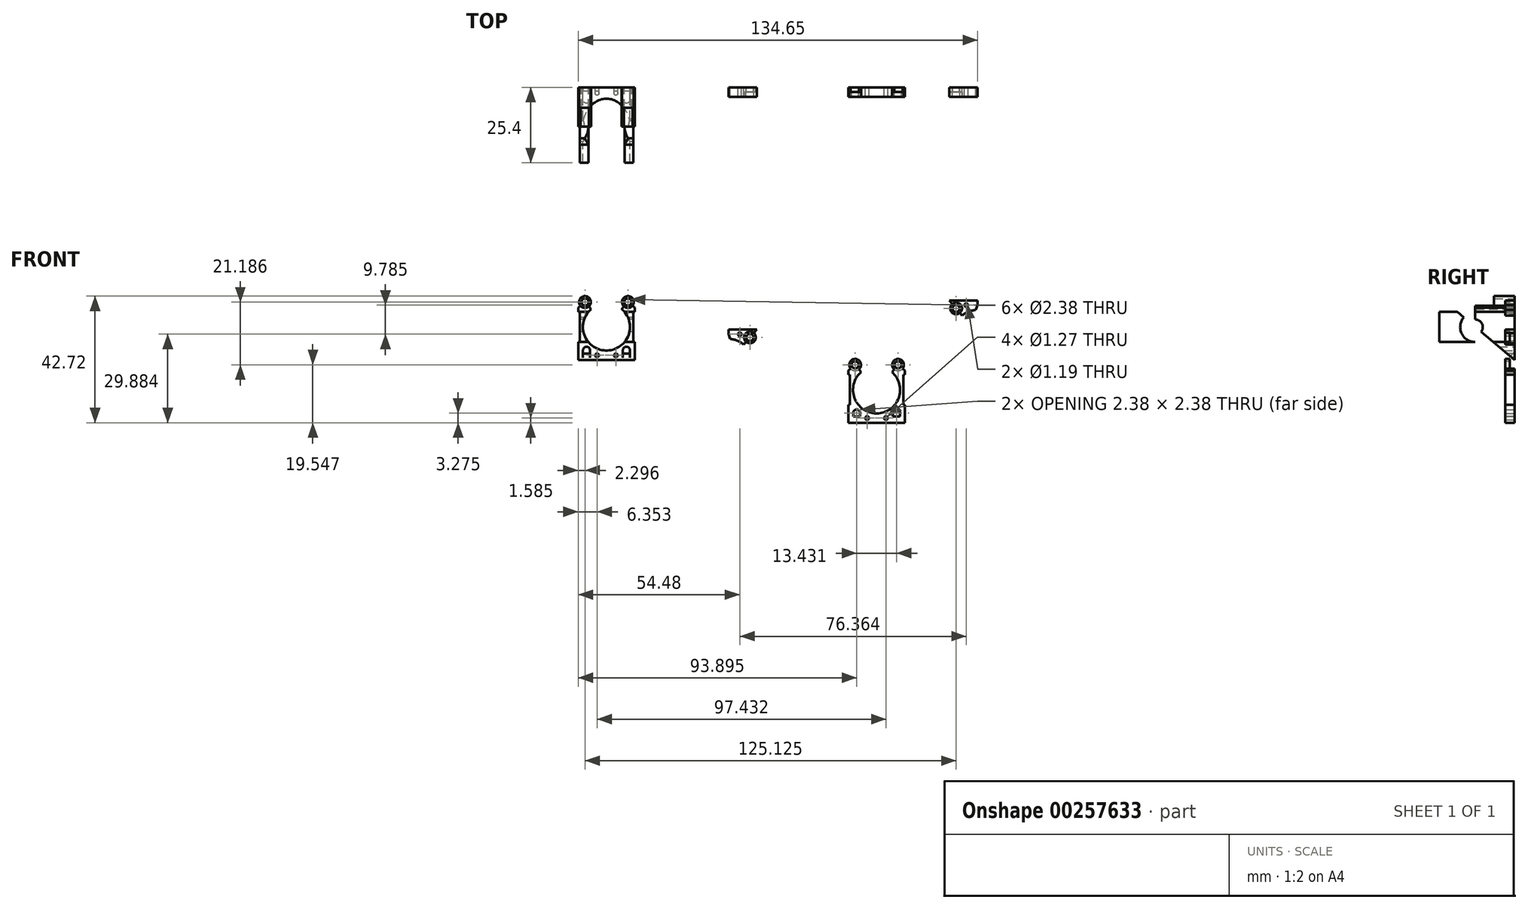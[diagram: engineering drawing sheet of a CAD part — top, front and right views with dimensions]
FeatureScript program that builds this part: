
annotation { "Feature Type Name" : "Feature", "Feature Type Description" : "" }
export const myFeature = defineFeature(function(context is Context, id is Id, definition is map)
    precondition{}
    {
        {
            var Q0;
            Q0=qCreatedBy(makeId("Front.planeOp"),FACE);
            var sketch = newSketch(context, id + "F0", { "sketchPlane" : qUnion([Q0])});
            skArc(sketch, "E0", {"start": v(-0.59, 7.92) * mm, "mid": v(0, -7.94) * mm, "end": v(0.59, 7.92) * mm});
            skCircle(sketch, "E1", {"center": v(0, 0) * mm, "radius": 9.53 * mm, "construction": true});
            skLineSegment(sketch, "E2", {"start": v(-12.11, 0) * mm, "end": v(13.66, 0) * mm, "construction": true});
            skLineSegment(sketch, "E3", {"start": v(0, 12.88) * mm, "end": v(0, -11.87) * mm, "construction": true});
            skLineSegment(sketch, "E4", {"start": v(7.94, 0) * mm, "end": v(7.94, 2.38) * mm, "construction": true});
            skLineSegment(sketch, "E5", {"start": v(9.53, 0) * mm, "end": v(9.53, 2.38) * mm, "construction": true});
            skLineSegment(sketch, "E6.bottom", {"start": v(-9.53, 0) * mm, "end": v(9.53, 0) * mm});
            skLineSegment(sketch, "E6.top", {"start": v(-9.53, 11.11) * mm, "end": v(9.53, 11.11) * mm});
            skLineSegment(sketch, "E6.right", {"start": v(9.53, 0) * mm, "end": v(9.53, 2.38) * mm});
            skLineSegment(sketch, "E7.top", {"start": v(-9.53, -11.11) * mm, "end": v(9.53, -11.11) * mm});
            skLineSegment(sketch, "E7.left", {"start": v(-9.53, -5.08) * mm, "end": v(-9.53, -11.11) * mm});
            skLineSegment(sketch, "E7.right", {"start": v(9.53, -5.08) * mm, "end": v(9.53, -11.11) * mm});
            skLineSegment(sketch, "E8", {"start": v(0, 9.53) * mm, "end": v(5.22, 9.53) * mm, "construction": true});
            skLineSegment(sketch, "E9", {"start": v(-3.97, -9.53) * mm, "end": v(0, -9.53) * mm, "construction": true});
            skLineSegment(sketch, "E10", {"start": v(0, 0) * mm, "end": v(-9.53, 11.11) * mm, "construction": true});
            skLineSegment(sketch, "E11", {"start": v(0, 0) * mm, "end": v(9.53, 11.11) * mm, "construction": true});
            skLineSegment(sketch, "E12", {"start": v(0, 0) * mm, "end": v(9.53, -11.11) * mm, "construction": true});
            skLineSegment(sketch, "E13", {"start": v(0, 0) * mm, "end": v(-9.53, -11.11) * mm, "construction": true});
            skCircle(sketch, "E14", {"center": v(0, 0) * mm, "radius": 11.11 * mm, "construction": true});
            skLineSegment(sketch, "E15", {"start": v(11.11, 0) * mm, "end": v(11.11, -2.7) * mm, "construction": true});
            skLineSegment(sketch, "E16", {"start": v(7.94, 0) * mm, "end": v(7.94, -2.67) * mm, "construction": true});
            skCircle(sketch, "E17", {"center": v(-7.23, 8.44) * mm, "radius": 1.2 * mm});
            skCircle(sketch, "E18", {"center": v(7.23, 8.44) * mm, "radius": 1.2 * mm});
            skCircle(sketch, "E19", {"center": v(-7.23, 8.44) * mm, "radius": 1.98 * mm});
            skCircle(sketch, "E20", {"center": v(7.23, 8.44) * mm, "radius": 1.98 * mm});
            skLineSegment(sketch, "E21", {"start": v(0, 9.53) * mm, "end": v(-5.07, 9.53) * mm, "construction": true});
            skCircle(sketch, "E22", {"center": v(-3.81, 9.53) * mm, "radius": 0.6 * mm});
            skCircle(sketch, "E23", {"center": v(3.81, 9.53) * mm, "radius": 0.6 * mm});
            skLineSegment(sketch, "E24", {"start": v(-7.23, 8.44) * mm, "end": v(-10.51, 5.63) * mm, "construction": true});
            skLineSegment(sketch, "E25", {"start": v(7.23, 8.44) * mm, "end": v(10.07, 6) * mm, "construction": true});
            skLineSegment(sketch, "E26", {"start": v(-7.23, 8.44) * mm, "end": v(-9.53, 11.11) * mm});
            skLineSegment(sketch, "E27", {"start": v(7.23, 8.44) * mm, "end": v(9.53, 11.11) * mm});
            skLineSegment(sketch, "E28", {"start": v(7.23, 8.44) * mm, "end": v(9.53, 6.47) * mm});
            skLineSegment(sketch, "E29", {"start": v(-7.23, 8.44) * mm, "end": v(-9.53, 6.47) * mm});
            skLineSegment(sketch, "E30", {"start": v(-7.23, 8.44) * mm, "end": v(-5.17, 6.03) * mm});
            skLineSegment(sketch, "E31", {"start": v(7.23, 8.44) * mm, "end": v(5.17, 6.03) * mm});
            skCircle(sketch, "E32", {"center": v(0, 0) * mm, "radius": 10.32 * mm, "construction": true});
            skLineSegment(sketch, "E33", {"start": v(0, -10.32) * mm, "end": v(2.62, -10.32) * mm, "construction": true});
            skCircle(sketch, "E34", {"center": v(6.72, -7.83) * mm, "radius": 1.2 * mm});
            skCircle(sketch, "E35", {"center": v(-6.72, -7.83) * mm, "radius": 1.2 * mm});
            skCircle(sketch, "E36", {"center": v(6.72, -7.83) * mm, "radius": 1.98 * mm});
            skCircle(sketch, "E37", {"center": v(-6.72, -7.83) * mm, "radius": 1.98 * mm});
            skLineSegment(sketch, "E38", {"start": v(-4.44, -7.83) * mm, "end": v(-9.1, -7.83) * mm, "construction": true});
            skLineSegment(sketch, "E39", {"start": v(8.94, -7.83) * mm, "end": v(4.4, -7.83) * mm, "construction": true});
            skLineSegment(sketch, "E40.bottom", {"start": v(-7.9, -7.83) * mm, "end": v(-6.72, -7.83) * mm});
            skLineSegment(sketch, "E40.top", {"start": v(-7.9, -9.03) * mm, "end": v(-6.72, -9.03) * mm});
            skLineSegment(sketch, "E40.left", {"start": v(-7.9, -7.83) * mm, "end": v(-7.9, -9.03) * mm});
            skLineSegment(sketch, "E40.right", {"start": v(-6.72, -7.83) * mm, "end": v(-6.72, -9.03) * mm});
            skLineSegment(sketch, "E41.bottom", {"start": v(-6.72, -9.03) * mm, "end": v(-5.52, -9.03) * mm});
            skLineSegment(sketch, "E41.top", {"start": v(-6.72, -7.83) * mm, "end": v(-5.52, -7.83) * mm});
            skLineSegment(sketch, "E41.left", {"start": v(-6.72, -9.03) * mm, "end": v(-6.72, -7.83) * mm});
            skLineSegment(sketch, "E41.right", {"start": v(-5.52, -9.03) * mm, "end": v(-5.52, -7.83) * mm});
            skLineSegment(sketch, "E42.bottom", {"start": v(5.52, -7.83) * mm, "end": v(6.72, -7.83) * mm});
            skLineSegment(sketch, "E42.top", {"start": v(5.52, -9.03) * mm, "end": v(6.72, -9.03) * mm});
            skLineSegment(sketch, "E42.left", {"start": v(5.52, -7.83) * mm, "end": v(5.52, -9.03) * mm});
            skLineSegment(sketch, "E42.right", {"start": v(6.72, -7.83) * mm, "end": v(6.72, -9.03) * mm});
            skLineSegment(sketch, "E43.bottom", {"start": v(6.72, -9.03) * mm, "end": v(7.9, -9.03) * mm});
            skLineSegment(sketch, "E43.top", {"start": v(6.72, -7.83) * mm, "end": v(7.9, -7.83) * mm});
            skLineSegment(sketch, "E43.left", {"start": v(6.72, -9.03) * mm, "end": v(6.72, -7.83) * mm});
            skLineSegment(sketch, "E43.right", {"start": v(7.9, -9.03) * mm, "end": v(7.9, -7.83) * mm});
            skLineSegment(sketch, "E44", {"start": v(0, -9.53) * mm, "end": v(4.87, -9.53) * mm, "construction": true});
            skCircle(sketch, "E45", {"center": v(-3.17, -9.53) * mm, "radius": 0.64 * mm});
            skCircle(sketch, "E46", {"center": v(3.18, -9.53) * mm, "radius": 0.64 * mm});
            skLineSegment(sketch, "E47", {"start": v(0, 9.53) * mm, "end": v(0.59, 7.92) * mm});
            skLineSegment(sketch, "E48", {"start": v(0, 9.53) * mm, "end": v(-0.59, 7.92) * mm});
            skLineSegment(sketch, "E49.bottom", {"start": v(-9.53, 5.08) * mm, "end": v(-9.02, 5.08) * mm});
            skLineSegment(sketch, "E49.top", {"start": v(-9.52, -5.08) * mm, "end": v(-9.02, -5.08) * mm});
            skLineSegment(sketch, "E49.right", {"start": v(-9.02, 5.08) * mm, "end": v(-9.02, -5.08) * mm});
            skPoint(sketch, "E50.firstSnap0", {"position": v(-9.27, 5.08) * mm});
            skLineSegment(sketch, "E50.bottom", {"start": v(9.53, 5.08) * mm, "end": v(9.02, 5.08) * mm});
            skLineSegment(sketch, "E50.top", {"start": v(9.52, -5.08) * mm, "end": v(9.02, -5.08) * mm});
            skLineSegment(sketch, "E50.right", {"start": v(9.02, 5.08) * mm, "end": v(9.02, -5.08) * mm});
            skLineSegment(sketch, "E51.trimOffspring", {"start": v(-9.53, 5.08) * mm, "end": v(-9.53, 6.47) * mm});
            skLineSegment(sketch, "E52.trimOffspring", {"start": v(9.53, 5.08) * mm, "end": v(9.53, 6.47) * mm});
            skLineSegment(sketch, "E53", {"start": v(0, 9.53) * mm, "end": v(0, 11.11) * mm});
            skSolve(sketch);
        }
        {
            var Q0;
            {var subQ7=sQuery(id+"F0.wireOp",EDGE,"E50.bottom");Q0=makeQuery(id+"F0.imprint","IMPRINT",FACE,{"disambiguationData":[TD([[makeQuery(id+"F0.imprint","IMPRINT",EDGE,{"derivedFrom":subQ7}),-1.0]])]});}
            var Q1;
            {var subQ12=sQuery(id+"F0.wireOp",EDGE,"E49.bottom");Q1=makeQuery(id+"F0.imprint","IMPRINT",FACE,{"disambiguationData":[TD([[makeQuery(id+"F0.imprint","IMPRINT",EDGE,{"derivedFrom":subQ12}),1.0]])]});}
            var Q2;
            Q2=makeQuery(id+"F0.imprint","IMPRINT",FACE,{"disambiguationData":[TD([[makeQuery(id+"F0.imprint","IMPRINT",EDGE,{"derivedFrom":sQuery(id+"F0.wireOp",EDGE,"E7.top")}),1.0]])]});
            var Q3;
            {var subQ0=sQuery(id+"F0.wireOp",EDGE,"E27");var subQ1=sQuery(id+"F0.wireOp",EDGE,"E18");var subQ2=makeQuery(id+"F0.imprint","INTERSECT",VERTEX,{"derivedFrom":[subQ1,subQ0]});Q3=makeQuery(id+"F0.imprint","IMPRINT",FACE,{"disambiguationData":[TD([[makeQuery(id+"F0.imprint","IMPRINT",EDGE,{"disambiguationData":[TD([[subQ2,1.0]])],"derivedFrom":subQ1}),-1.0]])]});}
            var Q4;
            {var subQ0=sQuery(id+"F0.wireOp",EDGE,"E31");var subQ1=sQuery(id+"F0.wireOp",EDGE,"E18");var subQ2=makeQuery(id+"F0.imprint","INTERSECT",VERTEX,{"derivedFrom":[subQ1,subQ0]});Q4=makeQuery(id+"F0.imprint","IMPRINT",FACE,{"disambiguationData":[TD([[makeQuery(id+"F0.imprint","IMPRINT",EDGE,{"disambiguationData":[TD([[subQ2,1.0]])],"derivedFrom":subQ1}),-1.0]])]});}
            var Q5;
            {var subQ0=sQuery(id+"F0.wireOp",EDGE,"E31");var subQ1=sQuery(id+"F0.wireOp",EDGE,"E18");var subQ2=makeQuery(id+"F0.imprint","INTERSECT",VERTEX,{"derivedFrom":[subQ1,subQ0]});Q5=makeQuery(id+"F0.imprint","IMPRINT",FACE,{"disambiguationData":[TD([[makeQuery(id+"F0.imprint","IMPRINT",EDGE,{"disambiguationData":[TD([[subQ2,-1.0]])],"derivedFrom":subQ1}),-1.0]])]});}
            var Q6;
            {var subQ0=sQuery(id+"F0.wireOp",EDGE,"E26");var subQ1=sQuery(id+"F0.wireOp",EDGE,"E17");var subQ2=makeQuery(id+"F0.imprint","INTERSECT",VERTEX,{"derivedFrom":[subQ1,subQ0]});Q6=makeQuery(id+"F0.imprint","IMPRINT",FACE,{"disambiguationData":[TD([[makeQuery(id+"F0.imprint","IMPRINT",EDGE,{"disambiguationData":[TD([[subQ2,1.0]])],"derivedFrom":subQ1}),-1.0]])]});}
            var Q7;
            {var subQ0=sQuery(id+"F0.wireOp",EDGE,"E29");var subQ1=sQuery(id+"F0.wireOp",EDGE,"E17");var subQ2=makeQuery(id+"F0.imprint","INTERSECT",VERTEX,{"derivedFrom":[subQ1,subQ0]});Q7=makeQuery(id+"F0.imprint","IMPRINT",FACE,{"disambiguationData":[TD([[makeQuery(id+"F0.imprint","IMPRINT",EDGE,{"disambiguationData":[TD([[subQ2,1.0]])],"derivedFrom":subQ1}),-1.0]])]});}
            var Q8;
            {var subQ0=sQuery(id+"F0.wireOp",EDGE,"E29");var subQ1=sQuery(id+"F0.wireOp",EDGE,"E17");var subQ2=makeQuery(id+"F0.imprint","INTERSECT",VERTEX,{"derivedFrom":[subQ1,subQ0]});Q8=makeQuery(id+"F0.imprint","IMPRINT",FACE,{"disambiguationData":[TD([[makeQuery(id+"F0.imprint","IMPRINT",EDGE,{"disambiguationData":[TD([[subQ2,-1.0]])],"derivedFrom":subQ1}),-1.0]])]});}
            var Q9;
            Q9=makeQuery(id+"F0.imprint","IMPRINT",FACE,{"disambiguationData":[TD([[makeQuery(id+"F0.imprint","IMPRINT",EDGE,{"derivedFrom":sQuery(id+"F0.wireOp",EDGE,"E37")}),1.0]])]});
            var Q10;
            Q10=makeQuery(id+"F0.imprint","IMPRINT",FACE,{"disambiguationData":[TD([[makeQuery(id+"F0.imprint","IMPRINT",EDGE,{"derivedFrom":sQuery(id+"F0.wireOp",EDGE,"E36")}),1.0]])]});
            extrude(context, id + "F1", {"entities" : qUnion([Q0, Q1, Q2, Q3, Q4, Q5, Q6, Q7, Q8, Q9, Q10]), "depth" : 3.17 * mm});
        }
        {
            var Q0;
            Q0=makeQuery(id+"F1.opExtrude","CAP_FACE",FACE,{"disambiguationData":[OSD([sQuery(id+"F0.wireOp",EDGE,"E0"),sQuery(id+"F0.wireOp",EDGE,"E7.top"),sQuery(id+"F0.wireOp",EDGE,"E7.left"),sQuery(id+"F0.wireOp",EDGE,"E7.right"),sQuery(id+"F0.wireOp",EDGE,"E17"),sQuery(id+"F0.wireOp",EDGE,"E18"),sQuery(id+"F0.wireOp",EDGE,"E19"),sQuery(id+"F0.wireOp",EDGE,"E20"),sQuery(id+"F0.wireOp",EDGE,"E28"),sQuery(id+"F0.wireOp",EDGE,"E29"),sQuery(id+"F0.wireOp",EDGE,"E30"),sQuery(id+"F0.wireOp",EDGE,"E31"),sQuery(id+"F0.wireOp",EDGE,"E34"),sQuery(id+"F0.wireOp",EDGE,"E35"),sQuery(id+"F0.wireOp",EDGE,"E40.top"),sQuery(id+"F0.wireOp",EDGE,"E40.left"),sQuery(id+"F0.wireOp",EDGE,"E41.bottom"),sQuery(id+"F0.wireOp",EDGE,"E41.right"),sQuery(id+"F0.wireOp",EDGE,"E42.top"),sQuery(id+"F0.wireOp",EDGE,"E42.left"),sQuery(id+"F0.wireOp",EDGE,"E43.bottom"),sQuery(id+"F0.wireOp",EDGE,"E43.right"),sQuery(id+"F0.wireOp",EDGE,"M6doSYil-dpmw-CiuU-3Rmr-2oMEXfOB3LK3"),sQuery(id+"F0.wireOp",EDGE,"LvhBBIzl-iPnS-g3sW-ETMN-LpCGhFxqwUK0"),sQuery(id+"F0.wireOp",EDGE,"E45"),sQuery(id+"F0.wireOp",EDGE,"E46"),sQuery(id+"F0.wireOp",EDGE,"E49.bottom"),sQuery(id+"F0.wireOp",EDGE,"E49.top"),sQuery(id+"F0.wireOp",EDGE,"E49.right"),sQuery(id+"F0.wireOp",EDGE,"E50.bottom"),sQuery(id+"F0.wireOp",EDGE,"E50.top"),sQuery(id+"F0.wireOp",EDGE,"E50.right"),sQuery(id+"F0.wireOp",EDGE,"E51.trimOffspring"),sQuery(id+"F0.wireOp",EDGE,"E52.trimOffspring")])],"isStart":true});
            var sketch = newSketch(context, id + "F2", { "sketchPlane" : qUnion([Q0])});
            skCircle(sketch, "E54", {"center": v(-7.23, 8.44) * mm, "radius": 1.98 * mm});
            skCircle(sketch, "E55", {"center": v(7.23, 8.44) * mm, "radius": 1.98 * mm});
            skSolve(sketch);
        }
        {
            var Q0;
            Q0 = qSketchRegion(id + "F2", true);
            extrude(context, id + "F3", {"entities" : qUnion([Q0]), "operationType" : NewBodyOperationType.REMOVE, "oppositeDirection" : true, "depth" : 1.59 * mm});
        }
        {
            var Q0;
            Q0=qCreatedBy(makeId("Front.planeOp"),FACE);
            var sketch = newSketch(context, id + "F4", { "sketchPlane" : qUnion([Q0])});
            skArc(sketch, "E56", {"start": v(-50.53, 17.17) * mm, "mid": v(-49.94, 1.31) * mm, "end": v(-49.35, 17.17) * mm});
            skCircle(sketch, "E57", {"center": v(-49.94, 9.25) * mm, "radius": 9.53 * mm, "construction": true});
            skLineSegment(sketch, "E58", {"start": v(-62.05, 9.25) * mm, "end": v(-36.28, 9.25) * mm, "construction": true});
            skLineSegment(sketch, "E59", {"start": v(-49.94, 22.13) * mm, "end": v(-49.94, -2.62) * mm, "construction": true});
            skLineSegment(sketch, "E60", {"start": v(-42, 9.25) * mm, "end": v(-42, 11.63) * mm, "construction": true});
            skLineSegment(sketch, "E61", {"start": v(-40.42, 9.25) * mm, "end": v(-40.42, 11.63) * mm, "construction": true});
            skLineSegment(sketch, "E62.bottom", {"start": v(-59.47, 9.25) * mm, "end": v(-40.42, 9.25) * mm});
            skLineSegment(sketch, "E62.top", {"start": v(-59.47, 20.36) * mm, "end": v(-40.42, 20.36) * mm});
            skLineSegment(sketch, "E62.right", {"start": v(-40.42, 9.25) * mm, "end": v(-40.42, 11.63) * mm});
            skLineSegment(sketch, "E63.top", {"start": v(-57.85, -1.86) * mm, "end": v(-42.03, -1.86) * mm});
            skLineSegment(sketch, "E63.left", {"start": v(-59.47, 4.17) * mm, "end": v(-59.47, -0.24) * mm});
            skLineSegment(sketch, "E63.right", {"start": v(-40.42, 4.17) * mm, "end": v(-40.42, -0.24) * mm});
            skLineSegment(sketch, "E64", {"start": v(-49.94, 18.77) * mm, "end": v(-44.72, 18.77) * mm, "construction": true});
            skLineSegment(sketch, "E65", {"start": v(-53.9, -0.28) * mm, "end": v(-49.94, -0.28) * mm, "construction": true});
            skLineSegment(sketch, "E66", {"start": v(-49.94, 9.25) * mm, "end": v(-59.47, 20.36) * mm, "construction": true});
            skLineSegment(sketch, "E67", {"start": v(-49.94, 9.25) * mm, "end": v(-40.42, 20.36) * mm, "construction": true});
            skLineSegment(sketch, "E68", {"start": v(-49.94, 9.25) * mm, "end": v(-40.42, -1.86) * mm, "construction": true});
            skLineSegment(sketch, "E69", {"start": v(-49.94, 9.25) * mm, "end": v(-59.47, -1.86) * mm, "construction": true});
            skCircle(sketch, "E70", {"center": v(-49.94, 9.25) * mm, "radius": 11.11 * mm, "construction": true});
            skLineSegment(sketch, "E71", {"start": v(-38.83, 9.25) * mm, "end": v(-38.83, 6.55) * mm, "construction": true});
            skLineSegment(sketch, "E72", {"start": v(-42, 9.25) * mm, "end": v(-42, 6.58) * mm, "construction": true});
            skCircle(sketch, "E73", {"center": v(-57.17, 17.69) * mm, "radius": 1.2 * mm});
            skCircle(sketch, "E74", {"center": v(-42.7, 17.69) * mm, "radius": 1.2 * mm});
            skCircle(sketch, "E75", {"center": v(-57.17, 17.69) * mm, "radius": 1.98 * mm});
            skCircle(sketch, "E76", {"center": v(-42.7, 17.69) * mm, "radius": 1.98 * mm});
            skLineSegment(sketch, "E77", {"start": v(-49.94, 18.77) * mm, "end": v(-55.01, 18.77) * mm, "construction": true});
            skCircle(sketch, "E78", {"center": v(-53.75, 18.77) * mm, "radius": 0.6 * mm});
            skCircle(sketch, "E79", {"center": v(-46.13, 18.77) * mm, "radius": 0.6 * mm});
            skLineSegment(sketch, "E80", {"start": v(-57.17, 17.69) * mm, "end": v(-60.45, 14.88) * mm, "construction": true});
            skLineSegment(sketch, "E81", {"start": v(-42.7, 17.69) * mm, "end": v(-39.87, 15.26) * mm, "construction": true});
            skLineSegment(sketch, "E82", {"start": v(-57.17, 17.69) * mm, "end": v(-59.47, 20.36) * mm});
            skLineSegment(sketch, "E83", {"start": v(-42.7, 17.69) * mm, "end": v(-40.42, 20.36) * mm});
            skLineSegment(sketch, "E84", {"start": v(-42.7, 17.69) * mm, "end": v(-40.42, 15.72) * mm});
            skLineSegment(sketch, "E85", {"start": v(-57.17, 17.69) * mm, "end": v(-59.47, 15.72) * mm});
            skLineSegment(sketch, "E86", {"start": v(-57.17, 17.69) * mm, "end": v(-55.1, 15.28) * mm});
            skLineSegment(sketch, "E87", {"start": v(-42.7, 17.69) * mm, "end": v(-44.77, 15.28) * mm});
            skCircle(sketch, "E88", {"center": v(-49.94, 9.25) * mm, "radius": 10.32 * mm, "construction": true});
            skLineSegment(sketch, "E89", {"start": v(-49.94, -1.07) * mm, "end": v(-47.32, -1.07) * mm, "construction": true});
            skCircle(sketch, "E90", {"center": v(-43.22, 1.41) * mm, "radius": 1.2 * mm});
            skCircle(sketch, "E91", {"center": v(-56.66, 1.41) * mm, "radius": 1.2 * mm});
            skCircle(sketch, "E92", {"center": v(-43.22, 1.41) * mm, "radius": 1.98 * mm});
            skCircle(sketch, "E93", {"center": v(-56.66, 1.41) * mm, "radius": 1.98 * mm});
            skLineSegment(sketch, "E94", {"start": v(-54.38, 1.41) * mm, "end": v(-59.04, 1.41) * mm, "construction": true});
            skLineSegment(sketch, "E95", {"start": v(-41, 1.41) * mm, "end": v(-45.53, 1.41) * mm, "construction": true});
            skLineSegment(sketch, "E96.bottom", {"start": v(-57.85, 1.41) * mm, "end": v(-56.66, 1.41) * mm});
            skLineSegment(sketch, "E96.top", {"start": v(-57.85, 0.22) * mm, "end": v(-56.66, 0.22) * mm});
            skLineSegment(sketch, "E96.left", {"start": v(-57.85, 1.41) * mm, "end": v(-57.85, 0.22) * mm});
            skLineSegment(sketch, "E96.right", {"start": v(-56.66, 1.41) * mm, "end": v(-56.66, 0.22) * mm});
            skLineSegment(sketch, "E97.bottom", {"start": v(-56.66, 0.22) * mm, "end": v(-55.46, 0.22) * mm});
            skLineSegment(sketch, "E97.top", {"start": v(-56.66, 1.41) * mm, "end": v(-55.46, 1.41) * mm});
            skLineSegment(sketch, "E97.left", {"start": v(-56.66, 0.22) * mm, "end": v(-56.66, 1.41) * mm});
            skLineSegment(sketch, "E97.right", {"start": v(-55.46, 0.22) * mm, "end": v(-55.46, 1.41) * mm});
            skLineSegment(sketch, "E98.bottom", {"start": v(-44.42, 1.41) * mm, "end": v(-43.22, 1.41) * mm});
            skLineSegment(sketch, "E98.top", {"start": v(-44.42, 0.22) * mm, "end": v(-43.22, 0.22) * mm});
            skLineSegment(sketch, "E98.left", {"start": v(-44.42, 1.41) * mm, "end": v(-44.42, 0.22) * mm});
            skLineSegment(sketch, "E98.right", {"start": v(-43.22, 1.41) * mm, "end": v(-43.22, 0.22) * mm});
            skLineSegment(sketch, "E99.bottom", {"start": v(-43.22, 0.22) * mm, "end": v(-42.03, 0.22) * mm});
            skLineSegment(sketch, "E99.top", {"start": v(-43.22, 1.41) * mm, "end": v(-42.03, 1.41) * mm});
            skLineSegment(sketch, "E99.left", {"start": v(-43.22, 0.22) * mm, "end": v(-43.22, 1.41) * mm});
            skLineSegment(sketch, "E99.right", {"start": v(-42.03, 0.22) * mm, "end": v(-42.03, 1.41) * mm});
            skLineSegment(sketch, "E100", {"start": v(-57.85, -1.86) * mm, "end": v(-59.47, -0.24) * mm});
            skLineSegment(sketch, "E101", {"start": v(-42.03, -1.86) * mm, "end": v(-40.42, -0.24) * mm});
            skLineSegment(sketch, "E102", {"start": v(-49.94, -0.28) * mm, "end": v(-45.07, -0.28) * mm, "construction": true});
            skCircle(sketch, "E103", {"center": v(-53.12, -0.28) * mm, "radius": 0.64 * mm});
            skCircle(sketch, "E104", {"center": v(-46.77, -0.28) * mm, "radius": 0.64 * mm});
            skLineSegment(sketch, "E105", {"start": v(-49.94, 18.77) * mm, "end": v(-49.35, 17.17) * mm});
            skLineSegment(sketch, "E106", {"start": v(-49.94, 18.77) * mm, "end": v(-50.53, 17.17) * mm});
            skLineSegment(sketch, "E107.bottom", {"start": v(-59.47, 14.33) * mm, "end": v(-58.96, 14.33) * mm});
            skLineSegment(sketch, "E107.top", {"start": v(-59.47, 4.17) * mm, "end": v(-58.96, 4.17) * mm});
            skLineSegment(sketch, "E107.right", {"start": v(-58.96, 14.33) * mm, "end": v(-58.96, 4.17) * mm});
            skPoint(sketch, "E108.firstSnap0", {"position": v(-59.21, 14.33) * mm});
            skLineSegment(sketch, "E108.bottom", {"start": v(-40.42, 14.33) * mm, "end": v(-40.92, 14.33) * mm});
            skLineSegment(sketch, "E108.top", {"start": v(-40.42, 4.17) * mm, "end": v(-40.92, 4.17) * mm});
            skLineSegment(sketch, "E108.right", {"start": v(-40.92, 14.33) * mm, "end": v(-40.92, 4.17) * mm});
            skLineSegment(sketch, "E109.trimOffspring", {"start": v(-59.47, 14.33) * mm, "end": v(-59.47, 15.72) * mm});
            skLineSegment(sketch, "E110.trimOffspring", {"start": v(-40.42, 14.33) * mm, "end": v(-40.42, 15.72) * mm});
            skLineSegment(sketch, "E111", {"start": v(-49.94, 18.77) * mm, "end": v(-49.94, 20.36) * mm});
            skSolve(sketch);
        }
        {
            var Q0;
            {var subQ0=sQuery(id+"F4.wireOp",EDGE,"E83");var subQ1=sQuery(id+"F4.wireOp",EDGE,"E74");var subQ2=makeQuery(id+"F4.imprint","INTERSECT",VERTEX,{"derivedFrom":[subQ1,subQ0]});Q0=makeQuery(id+"F4.imprint","IMPRINT",FACE,{"disambiguationData":[TD([[makeQuery(id+"F4.imprint","IMPRINT",EDGE,{"disambiguationData":[TD([[subQ2,1.0]])],"derivedFrom":subQ1}),-1.0]])]});}
            var Q1;
            {var subQ0=sQuery(id+"F4.wireOp",EDGE,"E87");var subQ1=sQuery(id+"F4.wireOp",EDGE,"E74");var subQ2=makeQuery(id+"F4.imprint","INTERSECT",VERTEX,{"derivedFrom":[subQ1,subQ0]});Q1=makeQuery(id+"F4.imprint","IMPRINT",FACE,{"disambiguationData":[TD([[makeQuery(id+"F4.imprint","IMPRINT",EDGE,{"disambiguationData":[TD([[subQ2,1.0]])],"derivedFrom":subQ1}),-1.0]])]});}
            var Q2;
            {var subQ0=sQuery(id+"F4.wireOp",EDGE,"E87");var subQ1=sQuery(id+"F4.wireOp",EDGE,"E74");var subQ2=makeQuery(id+"F4.imprint","INTERSECT",VERTEX,{"derivedFrom":[subQ1,subQ0]});Q2=makeQuery(id+"F4.imprint","IMPRINT",FACE,{"disambiguationData":[TD([[makeQuery(id+"F4.imprint","IMPRINT",EDGE,{"disambiguationData":[TD([[subQ2,-1.0]])],"derivedFrom":subQ1}),-1.0]])]});}
            var Q3;
            Q3=makeQuery(id+"F4.imprint","IMPRINT",FACE,{"disambiguationData":[TD([[makeQuery(id+"F4.imprint","IMPRINT",EDGE,{"derivedFrom":sQuery(id+"F4.wireOp",EDGE,"E79")}),-1.0]])]});
            extrude(context, id + "F5", {"entities" : qUnion([Q0, Q1, Q2, Q3]), "depth" : 3.17 * mm});
        }
        {
            var Q0;
            Q0=makeQuery(id+"F5.opExtrude","CAP_FACE",FACE,{"disambiguationData":[OSD([sQuery(id+"F4.wireOp",EDGE,"E56"),sQuery(id+"F4.wireOp",EDGE,"E62.top"),sQuery(id+"F4.wireOp",EDGE,"E74"),sQuery(id+"F4.wireOp",EDGE,"E76"),sQuery(id+"F4.wireOp",EDGE,"E79"),sQuery(id+"F4.wireOp",EDGE,"E83"),sQuery(id+"F4.wireOp",EDGE,"E87"),sQuery(id+"F4.wireOp",EDGE,"E105"),sQuery(id+"F4.wireOp",EDGE,"E111")])],"isStart":false});
            var sketch = newSketch(context, id + "F6", { "sketchPlane" : qUnion([Q0])});
            skCircle(sketch, "E112", {"center": v(-42.7, 17.69) * mm, "radius": 1.98 * mm});
            skSolve(sketch);
        }
        {
            var Q0;
            Q0 = qSketchRegion(id + "F6", true);
            extrude(context, id + "F7", {"entities" : qUnion([Q0]), "operationType" : NewBodyOperationType.REMOVE, "oppositeDirection" : true, "depth" : 1.59 * mm});
        }
        {
            var Q0;
            Q0=qCreatedBy(makeId("Front.planeOp"),FACE);
            var sketch = newSketch(context, id + "F8", { "sketchPlane" : qUnion([Q0])});
            skArc(sketch, "E113", {"start": v(33.46, 26.95) * mm, "mid": v(34.04, 11.1) * mm, "end": v(34.63, 26.95) * mm});
            skCircle(sketch, "E114", {"center": v(34.04, 19.03) * mm, "radius": 9.53 * mm, "construction": true});
            skLineSegment(sketch, "E115", {"start": v(21.93, 19.03) * mm, "end": v(47.7, 19.03) * mm, "construction": true});
            skLineSegment(sketch, "E116", {"start": v(34.04, 31.91) * mm, "end": v(34.04, 7.16) * mm, "construction": true});
            skLineSegment(sketch, "E117", {"start": v(41.98, 19.03) * mm, "end": v(41.98, 21.41) * mm, "construction": true});
            skLineSegment(sketch, "E118", {"start": v(43.57, 19.03) * mm, "end": v(43.57, 21.41) * mm, "construction": true});
            skLineSegment(sketch, "E119.bottom", {"start": v(24.52, 19.03) * mm, "end": v(43.57, 19.03) * mm});
            skLineSegment(sketch, "E119.top", {"start": v(24.52, 30.15) * mm, "end": v(43.57, 30.15) * mm});
            skLineSegment(sketch, "E119.right", {"start": v(43.57, 19.03) * mm, "end": v(43.57, 21.41) * mm});
            skLineSegment(sketch, "E120.top", {"start": v(26.14, 7.92) * mm, "end": v(41.95, 7.92) * mm});
            skLineSegment(sketch, "E120.left", {"start": v(24.52, 13.95) * mm, "end": v(24.52, 9.54) * mm});
            skLineSegment(sketch, "E120.right", {"start": v(43.57, 13.95) * mm, "end": v(43.57, 9.54) * mm});
            skLineSegment(sketch, "E121", {"start": v(34.04, 28.56) * mm, "end": v(39.27, 28.56) * mm, "construction": true});
            skLineSegment(sketch, "E122", {"start": v(30.07, 9.5) * mm, "end": v(34.04, 9.5) * mm, "construction": true});
            skLineSegment(sketch, "E123", {"start": v(34.04, 19.03) * mm, "end": v(24.52, 30.15) * mm, "construction": true});
            skLineSegment(sketch, "E124", {"start": v(34.04, 19.03) * mm, "end": v(43.57, 30.15) * mm, "construction": true});
            skLineSegment(sketch, "E125", {"start": v(34.04, 19.03) * mm, "end": v(43.57, 7.92) * mm, "construction": true});
            skLineSegment(sketch, "E126", {"start": v(34.04, 19.03) * mm, "end": v(24.52, 7.92) * mm, "construction": true});
            skCircle(sketch, "E127", {"center": v(34.04, 19.03) * mm, "radius": 11.11 * mm, "construction": true});
            skLineSegment(sketch, "E128", {"start": v(45.16, 19.03) * mm, "end": v(45.16, 16.34) * mm, "construction": true});
            skLineSegment(sketch, "E129", {"start": v(41.98, 19.03) * mm, "end": v(41.98, 16.36) * mm, "construction": true});
            skCircle(sketch, "E130", {"center": v(26.81, 27.47) * mm, "radius": 1.2 * mm});
            skCircle(sketch, "E131", {"center": v(41.28, 27.47) * mm, "radius": 1.2 * mm});
            skCircle(sketch, "E132", {"center": v(26.81, 27.47) * mm, "radius": 1.98 * mm});
            skCircle(sketch, "E133", {"center": v(41.28, 27.47) * mm, "radius": 1.98 * mm});
            skLineSegment(sketch, "E134", {"start": v(34.04, 28.56) * mm, "end": v(28.97, 28.56) * mm, "construction": true});
            skCircle(sketch, "E135", {"center": v(30.23, 28.56) * mm, "radius": 0.6 * mm});
            skCircle(sketch, "E136", {"center": v(37.85, 28.56) * mm, "radius": 0.6 * mm});
            skLineSegment(sketch, "E137", {"start": v(26.81, 27.47) * mm, "end": v(23.53, 24.66) * mm, "construction": true});
            skLineSegment(sketch, "E138", {"start": v(41.28, 27.47) * mm, "end": v(44.11, 25.04) * mm, "construction": true});
            skLineSegment(sketch, "E139", {"start": v(26.81, 27.47) * mm, "end": v(24.52, 30.15) * mm});
            skLineSegment(sketch, "E140", {"start": v(41.28, 27.47) * mm, "end": v(43.57, 30.15) * mm});
            skLineSegment(sketch, "E141", {"start": v(41.28, 27.47) * mm, "end": v(43.57, 25.5) * mm});
            skLineSegment(sketch, "E142", {"start": v(26.81, 27.47) * mm, "end": v(24.52, 25.5) * mm});
            skLineSegment(sketch, "E143", {"start": v(26.81, 27.47) * mm, "end": v(28.88, 25.06) * mm});
            skLineSegment(sketch, "E144", {"start": v(41.28, 27.47) * mm, "end": v(39.2, 25.06) * mm});
            skCircle(sketch, "E145", {"center": v(34.04, 19.03) * mm, "radius": 10.32 * mm, "construction": true});
            skLineSegment(sketch, "E146", {"start": v(34.04, 8.72) * mm, "end": v(36.66, 8.72) * mm, "construction": true});
            skCircle(sketch, "E147", {"center": v(40.76, 11.2) * mm, "radius": 1.2 * mm});
            skCircle(sketch, "E148", {"center": v(27.33, 11.2) * mm, "radius": 1.2 * mm});
            skCircle(sketch, "E149", {"center": v(40.76, 11.2) * mm, "radius": 1.98 * mm});
            skCircle(sketch, "E150", {"center": v(27.33, 11.2) * mm, "radius": 1.98 * mm});
            skLineSegment(sketch, "E151", {"start": v(29.6, 11.2) * mm, "end": v(24.95, 11.2) * mm, "construction": true});
            skLineSegment(sketch, "E152", {"start": v(42.99, 11.2) * mm, "end": v(38.45, 11.2) * mm, "construction": true});
            skLineSegment(sketch, "E153.bottom", {"start": v(26.14, 11.2) * mm, "end": v(27.33, 11.2) * mm});
            skLineSegment(sketch, "E153.top", {"start": v(26.14, 10) * mm, "end": v(27.33, 10) * mm});
            skLineSegment(sketch, "E153.left", {"start": v(26.14, 11.2) * mm, "end": v(26.14, 10) * mm});
            skLineSegment(sketch, "E153.right", {"start": v(27.33, 11.2) * mm, "end": v(27.33, 10) * mm});
            skLineSegment(sketch, "E154.bottom", {"start": v(27.33, 10) * mm, "end": v(28.52, 10) * mm});
            skLineSegment(sketch, "E154.top", {"start": v(27.33, 11.2) * mm, "end": v(28.52, 11.2) * mm});
            skLineSegment(sketch, "E154.left", {"start": v(27.33, 10) * mm, "end": v(27.33, 11.2) * mm});
            skLineSegment(sketch, "E154.right", {"start": v(28.52, 10) * mm, "end": v(28.52, 11.2) * mm});
            skLineSegment(sketch, "E155.bottom", {"start": v(39.57, 11.2) * mm, "end": v(40.76, 11.2) * mm});
            skLineSegment(sketch, "E155.top", {"start": v(39.57, 10) * mm, "end": v(40.76, 10) * mm});
            skLineSegment(sketch, "E155.left", {"start": v(39.57, 11.2) * mm, "end": v(39.57, 10) * mm});
            skLineSegment(sketch, "E155.right", {"start": v(40.76, 11.2) * mm, "end": v(40.76, 10) * mm});
            skLineSegment(sketch, "E156.bottom", {"start": v(40.76, 10) * mm, "end": v(41.95, 10) * mm});
            skLineSegment(sketch, "E156.top", {"start": v(40.76, 11.2) * mm, "end": v(41.95, 11.2) * mm});
            skLineSegment(sketch, "E156.left", {"start": v(40.76, 10) * mm, "end": v(40.76, 11.2) * mm});
            skLineSegment(sketch, "E156.right", {"start": v(41.95, 10) * mm, "end": v(41.95, 11.2) * mm});
            skLineSegment(sketch, "E157", {"start": v(26.14, 7.92) * mm, "end": v(24.52, 9.54) * mm});
            skLineSegment(sketch, "E158", {"start": v(41.95, 7.92) * mm, "end": v(43.57, 9.54) * mm});
            skLineSegment(sketch, "E159", {"start": v(34.04, 9.5) * mm, "end": v(38.91, 9.5) * mm, "construction": true});
            skCircle(sketch, "E160", {"center": v(30.87, 9.5) * mm, "radius": 0.64 * mm});
            skCircle(sketch, "E161", {"center": v(37.22, 9.5) * mm, "radius": 0.64 * mm});
            skLineSegment(sketch, "E162", {"start": v(34.04, 28.56) * mm, "end": v(34.63, 26.95) * mm});
            skLineSegment(sketch, "E163", {"start": v(34.04, 28.56) * mm, "end": v(33.46, 26.95) * mm});
            skLineSegment(sketch, "E164.bottom", {"start": v(24.52, 24.11) * mm, "end": v(25.03, 24.11) * mm});
            skLineSegment(sketch, "E164.top", {"start": v(24.52, 13.95) * mm, "end": v(25.03, 13.95) * mm});
            skLineSegment(sketch, "E164.right", {"start": v(25.03, 24.11) * mm, "end": v(25.03, 13.95) * mm});
            skPoint(sketch, "E165.firstSnap0", {"position": v(24.77, 24.11) * mm});
            skLineSegment(sketch, "E165.bottom", {"start": v(43.57, 24.11) * mm, "end": v(43.06, 24.11) * mm});
            skLineSegment(sketch, "E165.top", {"start": v(43.57, 13.95) * mm, "end": v(43.06, 13.95) * mm});
            skLineSegment(sketch, "E165.right", {"start": v(43.06, 24.11) * mm, "end": v(43.06, 13.95) * mm});
            skLineSegment(sketch, "E166.trimOffspring", {"start": v(24.52, 24.11) * mm, "end": v(24.52, 25.5) * mm});
            skLineSegment(sketch, "E167.trimOffspring", {"start": v(43.57, 24.11) * mm, "end": v(43.57, 25.5) * mm});
            skLineSegment(sketch, "E168", {"start": v(34.04, 28.56) * mm, "end": v(34.04, 30.15) * mm});
            skSolve(sketch);
        }
        {
            var Q0;
            {var subQ0=sQuery(id+"F8.wireOp",EDGE,"E142");var subQ1=sQuery(id+"F8.wireOp",EDGE,"E130");var subQ2=makeQuery(id+"F8.imprint","INTERSECT",VERTEX,{"derivedFrom":[subQ1,subQ0]});Q0=makeQuery(id+"F8.imprint","IMPRINT",FACE,{"disambiguationData":[TD([[makeQuery(id+"F8.imprint","IMPRINT",EDGE,{"disambiguationData":[TD([[subQ2,1.0]])],"derivedFrom":subQ1}),-1.0]])]});}
            var Q1;
            {var subQ0=sQuery(id+"F8.wireOp",EDGE,"E142");var subQ1=sQuery(id+"F8.wireOp",EDGE,"E130");var subQ2=makeQuery(id+"F8.imprint","INTERSECT",VERTEX,{"derivedFrom":[subQ1,subQ0]});Q1=makeQuery(id+"F8.imprint","IMPRINT",FACE,{"disambiguationData":[TD([[makeQuery(id+"F8.imprint","IMPRINT",EDGE,{"disambiguationData":[TD([[subQ2,-1.0]])],"derivedFrom":subQ1}),-1.0]])]});}
            var Q2;
            {var subQ0=sQuery(id+"F8.wireOp",EDGE,"E139");var subQ1=sQuery(id+"F8.wireOp",EDGE,"E130");var subQ2=makeQuery(id+"F8.imprint","INTERSECT",VERTEX,{"derivedFrom":[subQ1,subQ0]});Q2=makeQuery(id+"F8.imprint","IMPRINT",FACE,{"disambiguationData":[TD([[makeQuery(id+"F8.imprint","IMPRINT",EDGE,{"disambiguationData":[TD([[subQ2,1.0]])],"derivedFrom":subQ1}),-1.0]])]});}
            var Q3;
            Q3=makeQuery(id+"F8.imprint","IMPRINT",FACE,{"disambiguationData":[TD([[makeQuery(id+"F8.imprint","IMPRINT",EDGE,{"derivedFrom":sQuery(id+"F8.wireOp",EDGE,"E135")}),-1.0]])]});
            extrude(context, id + "F9", {"entities" : qUnion([Q0, Q1, Q2, Q3]), "depth" : 3.17 * mm});
        }
        {
            var Q0;
            Q0=makeQuery(id+"F9.opExtrude","CAP_FACE",FACE,{"disambiguationData":[OSD([sQuery(id+"F8.wireOp",EDGE,"E113"),sQuery(id+"F8.wireOp",EDGE,"E119.top"),sQuery(id+"F8.wireOp",EDGE,"E130"),sQuery(id+"F8.wireOp",EDGE,"E132"),sQuery(id+"F8.wireOp",EDGE,"E135"),sQuery(id+"F8.wireOp",EDGE,"E139"),sQuery(id+"F8.wireOp",EDGE,"E143"),sQuery(id+"F8.wireOp",EDGE,"E163"),sQuery(id+"F8.wireOp",EDGE,"E168")])],"isStart":false});
            var sketch = newSketch(context, id + "F10", { "sketchPlane" : qUnion([Q0])});
            skCircle(sketch, "E169", {"center": v(26.81, 27.47) * mm, "radius": 1.98 * mm});
            skSolve(sketch);
        }
        {
            var Q0;
            Q0 = qSketchRegion(id + "F10", true);
            extrude(context, id + "F11", {"entities" : qUnion([Q0]), "operationType" : NewBodyOperationType.REMOVE, "oppositeDirection" : true, "depth" : 1.59 * mm});
        }
        {
            var Q0;
            Q0=qCreatedBy(makeId("Front.planeOp"),FACE);
            var sketch = newSketch(context, id + "F12", { "sketchPlane" : qUnion([Q0])});
            skArc(sketch, "E170", {"start": v(-91.67, 29.1) * mm, "mid": v(-91.08, 13.25) * mm, "end": v(-90.5, 29.1) * mm});
            skCircle(sketch, "E171", {"center": v(-91.08, 21.19) * mm, "radius": 9.53 * mm, "construction": true});
            skLineSegment(sketch, "E172", {"start": v(-103.2, 21.19) * mm, "end": v(-77.43, 21.19) * mm, "construction": true});
            skLineSegment(sketch, "E173", {"start": v(-91.08, 34.06) * mm, "end": v(-91.08, 9.32) * mm, "construction": true});
            skLineSegment(sketch, "E174", {"start": v(-83.14, 21.19) * mm, "end": v(-83.14, 23.56) * mm, "construction": true});
            skLineSegment(sketch, "E175", {"start": v(-81.56, 21.19) * mm, "end": v(-81.56, 23.56) * mm, "construction": true});
            skLineSegment(sketch, "E176.bottom", {"start": v(-100.6, 21.19) * mm, "end": v(-81.56, 21.19) * mm});
            skLineSegment(sketch, "E176.top", {"start": v(-100.6, 32.3) * mm, "end": v(-81.56, 32.3) * mm});
            skLineSegment(sketch, "E176.right", {"start": v(-81.56, 21.19) * mm, "end": v(-81.56, 23.56) * mm});
            skLineSegment(sketch, "E177.top", {"start": v(-100.6, 10.07) * mm, "end": v(-81.56, 10.07) * mm});
            skLineSegment(sketch, "E177.left", {"start": v(-100.6, 16.1) * mm, "end": v(-100.6, 10.07) * mm});
            skLineSegment(sketch, "E177.right", {"start": v(-81.56, 16.1) * mm, "end": v(-81.56, 10.07) * mm});
            skLineSegment(sketch, "E178", {"start": v(-91.08, 30.71) * mm, "end": v(-85.86, 30.71) * mm, "construction": true});
            skLineSegment(sketch, "E179", {"start": v(-95.05, 11.66) * mm, "end": v(-91.08, 11.66) * mm, "construction": true});
            skLineSegment(sketch, "E180", {"start": v(-91.08, 21.19) * mm, "end": v(-100.6, 32.3) * mm, "construction": true});
            skLineSegment(sketch, "E181", {"start": v(-91.08, 21.19) * mm, "end": v(-81.56, 32.3) * mm, "construction": true});
            skLineSegment(sketch, "E182", {"start": v(-91.08, 21.19) * mm, "end": v(-81.56, 10.07) * mm, "construction": true});
            skLineSegment(sketch, "E183", {"start": v(-91.08, 21.19) * mm, "end": v(-100.6, 10.07) * mm, "construction": true});
            skCircle(sketch, "E184", {"center": v(-91.08, 21.19) * mm, "radius": 11.11 * mm, "construction": true});
            skLineSegment(sketch, "E185", {"start": v(-79.97, 21.19) * mm, "end": v(-79.97, 18.5) * mm, "construction": true});
            skLineSegment(sketch, "E186", {"start": v(-83.14, 21.19) * mm, "end": v(-83.14, 18.51) * mm, "construction": true});
            skCircle(sketch, "E187", {"center": v(-98.31, 29.62) * mm, "radius": 1.2 * mm});
            skCircle(sketch, "E188", {"center": v(-83.85, 29.62) * mm, "radius": 1.2 * mm});
            skCircle(sketch, "E189", {"center": v(-98.31, 29.62) * mm, "radius": 1.98 * mm});
            skCircle(sketch, "E190", {"center": v(-83.85, 29.62) * mm, "radius": 1.98 * mm});
            skLineSegment(sketch, "E191", {"start": v(-91.08, 30.71) * mm, "end": v(-96.15, 30.71) * mm, "construction": true});
            skCircle(sketch, "E192", {"center": v(-94.9, 30.71) * mm, "radius": 0.6 * mm});
            skCircle(sketch, "E193", {"center": v(-87.27, 30.71) * mm, "radius": 0.6 * mm});
            skLineSegment(sketch, "E194", {"start": v(-98.31, 29.62) * mm, "end": v(-101.6, 26.81) * mm, "construction": true});
            skLineSegment(sketch, "E195", {"start": v(-83.85, 29.62) * mm, "end": v(-81.01, 27.2) * mm, "construction": true});
            skLineSegment(sketch, "E196", {"start": v(-98.31, 29.62) * mm, "end": v(-100.6, 32.3) * mm});
            skLineSegment(sketch, "E197", {"start": v(-83.85, 29.62) * mm, "end": v(-81.56, 32.3) * mm});
            skLineSegment(sketch, "E198", {"start": v(-83.85, 29.62) * mm, "end": v(-81.56, 27.66) * mm});
            skLineSegment(sketch, "E199", {"start": v(-98.31, 29.62) * mm, "end": v(-100.6, 27.66) * mm});
            skLineSegment(sketch, "E200", {"start": v(-98.31, 29.62) * mm, "end": v(-96.25, 27.21) * mm});
            skLineSegment(sketch, "E201", {"start": v(-83.85, 29.62) * mm, "end": v(-85.92, 27.21) * mm});
            skCircle(sketch, "E202", {"center": v(-91.08, 21.19) * mm, "radius": 10.32 * mm, "construction": true});
            skLineSegment(sketch, "E203", {"start": v(-91.08, 10.87) * mm, "end": v(-88.46, 10.87) * mm, "construction": true});
            skCircle(sketch, "E204", {"center": v(-84.37, 13.35) * mm, "radius": 1.2 * mm});
            skCircle(sketch, "E205", {"center": v(-97.8, 13.35) * mm, "radius": 1.2 * mm});
            skCircle(sketch, "E206", {"center": v(-84.37, 13.35) * mm, "radius": 1.98 * mm});
            skCircle(sketch, "E207", {"center": v(-97.8, 13.35) * mm, "radius": 1.98 * mm});
            skLineSegment(sketch, "E208", {"start": v(-95.52, 13.35) * mm, "end": v(-100.18, 13.35) * mm, "construction": true});
            skLineSegment(sketch, "E209", {"start": v(-82.14, 13.35) * mm, "end": v(-86.67, 13.35) * mm, "construction": true});
            skLineSegment(sketch, "E210.bottom", {"start": v(-98.99, 13.35) * mm, "end": v(-97.8, 13.35) * mm});
            skLineSegment(sketch, "E210.top", {"start": v(-98.99, 12.16) * mm, "end": v(-97.8, 12.16) * mm});
            skLineSegment(sketch, "E210.left", {"start": v(-98.99, 13.35) * mm, "end": v(-98.99, 12.16) * mm});
            skLineSegment(sketch, "E210.right", {"start": v(-97.8, 13.35) * mm, "end": v(-97.8, 12.16) * mm});
            skLineSegment(sketch, "E211.bottom", {"start": v(-97.8, 12.16) * mm, "end": v(-96.6, 12.16) * mm});
            skLineSegment(sketch, "E211.top", {"start": v(-97.8, 13.35) * mm, "end": v(-96.6, 13.35) * mm});
            skLineSegment(sketch, "E211.left", {"start": v(-97.8, 12.16) * mm, "end": v(-97.8, 13.35) * mm});
            skLineSegment(sketch, "E211.right", {"start": v(-96.6, 12.16) * mm, "end": v(-96.6, 13.35) * mm});
            skLineSegment(sketch, "E212.bottom", {"start": v(-85.56, 13.35) * mm, "end": v(-84.37, 13.35) * mm});
            skLineSegment(sketch, "E212.top", {"start": v(-85.56, 12.16) * mm, "end": v(-84.37, 12.16) * mm});
            skLineSegment(sketch, "E212.left", {"start": v(-85.56, 13.35) * mm, "end": v(-85.56, 12.16) * mm});
            skLineSegment(sketch, "E212.right", {"start": v(-84.37, 13.35) * mm, "end": v(-84.37, 12.16) * mm});
            skLineSegment(sketch, "E213.bottom", {"start": v(-84.37, 12.16) * mm, "end": v(-83.18, 12.16) * mm});
            skLineSegment(sketch, "E213.top", {"start": v(-84.37, 13.35) * mm, "end": v(-83.18, 13.35) * mm});
            skLineSegment(sketch, "E213.left", {"start": v(-84.37, 12.16) * mm, "end": v(-84.37, 13.35) * mm});
            skLineSegment(sketch, "E213.right", {"start": v(-83.18, 12.16) * mm, "end": v(-83.18, 13.35) * mm});
            skLineSegment(sketch, "E214", {"start": v(-91.08, 11.66) * mm, "end": v(-86.21, 11.66) * mm, "construction": true});
            skCircle(sketch, "E215", {"center": v(-94.26, 11.66) * mm, "radius": 0.64 * mm});
            skCircle(sketch, "E216", {"center": v(-87.9, 11.66) * mm, "radius": 0.64 * mm});
            skLineSegment(sketch, "E217", {"start": v(-91.08, 30.71) * mm, "end": v(-90.5, 29.1) * mm});
            skLineSegment(sketch, "E218", {"start": v(-91.08, 30.71) * mm, "end": v(-91.67, 29.1) * mm});
            skLineSegment(sketch, "E219.bottom", {"start": v(-100.6, 26.27) * mm, "end": v(-100.1, 26.27) * mm});
            skLineSegment(sketch, "E219.top", {"start": v(-100.6, 16.1) * mm, "end": v(-100.1, 16.1) * mm});
            skLineSegment(sketch, "E219.right", {"start": v(-100.1, 26.27) * mm, "end": v(-100.1, 16.1) * mm});
            skPoint(sketch, "E220.firstSnap0", {"position": v(-100.35, 26.27) * mm});
            skLineSegment(sketch, "E220.bottom", {"start": v(-81.56, 26.27) * mm, "end": v(-82.07, 26.27) * mm});
            skLineSegment(sketch, "E220.top", {"start": v(-81.56, 16.1) * mm, "end": v(-82.07, 16.1) * mm});
            skLineSegment(sketch, "E220.right", {"start": v(-82.07, 26.27) * mm, "end": v(-82.07, 16.1) * mm});
            skLineSegment(sketch, "E221.trimOffspring", {"start": v(-100.6, 26.27) * mm, "end": v(-100.6, 27.66) * mm});
            skLineSegment(sketch, "E222.trimOffspring", {"start": v(-81.56, 26.27) * mm, "end": v(-81.56, 27.66) * mm});
            skLineSegment(sketch, "E223", {"start": v(-91.08, 30.71) * mm, "end": v(-91.08, 32.3) * mm});
            skSolve(sketch);
        }
        {
            var Q0;
            {var subQ0=sQuery(id+"F12.wireOp",EDGE,"E199");var subQ1=sQuery(id+"F12.wireOp",EDGE,"E187");var subQ2=makeQuery(id+"F12.imprint","INTERSECT",VERTEX,{"derivedFrom":[subQ1,subQ0]});Q0=makeQuery(id+"F12.imprint","IMPRINT",FACE,{"disambiguationData":[TD([[makeQuery(id+"F12.imprint","IMPRINT",EDGE,{"disambiguationData":[TD([[subQ2,1.0]])],"derivedFrom":subQ1}),-1.0]])]});}
            var Q1;
            {var subQ0=sQuery(id+"F12.wireOp",EDGE,"E197");var subQ1=sQuery(id+"F12.wireOp",EDGE,"E188");var subQ2=makeQuery(id+"F12.imprint","INTERSECT",VERTEX,{"derivedFrom":[subQ1,subQ0]});Q1=makeQuery(id+"F12.imprint","IMPRINT",FACE,{"disambiguationData":[TD([[makeQuery(id+"F12.imprint","IMPRINT",EDGE,{"disambiguationData":[TD([[subQ2,1.0]])],"derivedFrom":subQ1}),-1.0]])]});}
            var Q2;
            {var subQ6=sQuery(id+"F12.wireOp",EDGE,"E219.bottom");Q2=makeQuery(id+"F12.imprint","IMPRINT",FACE,{"disambiguationData":[TD([[makeQuery(id+"F12.imprint","IMPRINT",EDGE,{"derivedFrom":subQ6}),1.0]])]});}
            var Q3;
            {var subQ12=sQuery(id+"F12.wireOp",EDGE,"E220.bottom");Q3=makeQuery(id+"F12.imprint","IMPRINT",FACE,{"disambiguationData":[TD([[makeQuery(id+"F12.imprint","IMPRINT",EDGE,{"derivedFrom":subQ12}),-1.0]])]});}
            var Q4;
            {var subQ0=sQuery(id+"F12.wireOp",EDGE,"E199");var subQ1=sQuery(id+"F12.wireOp",EDGE,"E187");var subQ2=makeQuery(id+"F12.imprint","INTERSECT",VERTEX,{"derivedFrom":[subQ1,subQ0]});Q4=makeQuery(id+"F12.imprint","IMPRINT",FACE,{"disambiguationData":[TD([[makeQuery(id+"F12.imprint","IMPRINT",EDGE,{"disambiguationData":[TD([[subQ2,-1.0]])],"derivedFrom":subQ1}),-1.0]])]});}
            var Q5;
            {var subQ0=sQuery(id+"F12.wireOp",EDGE,"E196");var subQ1=sQuery(id+"F12.wireOp",EDGE,"E187");var subQ2=makeQuery(id+"F12.imprint","INTERSECT",VERTEX,{"derivedFrom":[subQ1,subQ0]});Q5=makeQuery(id+"F12.imprint","IMPRINT",FACE,{"disambiguationData":[TD([[makeQuery(id+"F12.imprint","IMPRINT",EDGE,{"disambiguationData":[TD([[subQ2,1.0]])],"derivedFrom":subQ1}),-1.0]])]});}
            var Q6;
            {var subQ0=sQuery(id+"F12.wireOp",EDGE,"E201");var subQ1=sQuery(id+"F12.wireOp",EDGE,"E188");var subQ2=makeQuery(id+"F12.imprint","INTERSECT",VERTEX,{"derivedFrom":[subQ1,subQ0]});Q6=makeQuery(id+"F12.imprint","IMPRINT",FACE,{"disambiguationData":[TD([[makeQuery(id+"F12.imprint","IMPRINT",EDGE,{"disambiguationData":[TD([[subQ2,1.0]])],"derivedFrom":subQ1}),-1.0]])]});}
            var Q7;
            {var subQ0=sQuery(id+"F12.wireOp",EDGE,"E201");var subQ1=sQuery(id+"F12.wireOp",EDGE,"E188");var subQ2=makeQuery(id+"F12.imprint","INTERSECT",VERTEX,{"derivedFrom":[subQ1,subQ0]});Q7=makeQuery(id+"F12.imprint","IMPRINT",FACE,{"disambiguationData":[TD([[makeQuery(id+"F12.imprint","IMPRINT",EDGE,{"disambiguationData":[TD([[subQ2,-1.0]])],"derivedFrom":subQ1}),-1.0]])]});}
            var Q8;
            Q8=makeQuery(id+"F12.imprint","IMPRINT",FACE,{"disambiguationData":[TD([[makeQuery(id+"F12.imprint","IMPRINT",EDGE,{"derivedFrom":sQuery(id+"F12.wireOp",EDGE,"E177.top")}),1.0]])]});
            var Q9;
            Q9=makeQuery(id+"F12.imprint","IMPRINT",FACE,{"disambiguationData":[TD([[makeQuery(id+"F12.imprint","IMPRINT",EDGE,{"derivedFrom":sQuery(id+"F12.wireOp",EDGE,"E206")}),1.0]])]});
            var Q10;
            Q10=makeQuery(id+"F12.imprint","IMPRINT",FACE,{"disambiguationData":[TD([[makeQuery(id+"F12.imprint","IMPRINT",EDGE,{"derivedFrom":sQuery(id+"F12.wireOp",EDGE,"E207")}),1.0]])]});
            extrude(context, id + "F13", {"entities" : qUnion([Q0, Q1, Q2, Q3, Q4, Q5, Q6, Q7, Q8, Q9, Q10]), "depth" : 25.4 * mm});
        }
        {
            var Q0;
            Q0=makeQuery(id+"F13.opExtrude","SWEPT_FACE",FACE,{"disambiguationData":[OSD([sQuery(id+"F12.wireOp",EDGE,"E177.left")])]});
            var sketch = newSketch(context, id + "F14", { "sketchPlane" : qUnion([Q0])});
            skLineSegment(sketch, "E224.bottom", {"start": v(0, 10.07) * mm, "end": v(26.46, 10.07) * mm});
            skLineSegment(sketch, "E224.top", {"start": v(0, 32.62) * mm, "end": v(26.46, 32.62) * mm});
            skLineSegment(sketch, "E224.left", {"start": v(0, 10.07) * mm, "end": v(0, 32.62) * mm});
            skLineSegment(sketch, "E224.right", {"start": v(26.46, 10.07) * mm, "end": v(26.46, 32.62) * mm});
            skLineSegment(sketch, "E225", {"start": v(0, 10.07) * mm, "end": v(26.87, 32.62) * mm});
            skLineSegment(sketch, "E226.bottom", {"start": v(0, 16.1) * mm, "end": v(26.46, 16.1) * mm});
            skLineSegment(sketch, "E226.top", {"start": v(0, 26.27) * mm, "end": v(26.46, 26.27) * mm});
            skLineSegment(sketch, "E226.left", {"start": v(0, 16.1) * mm, "end": v(0, 26.27) * mm});
            skLineSegment(sketch, "E226.right", {"start": v(26.46, 16.1) * mm, "end": v(26.46, 26.27) * mm});
            skLineSegment(sketch, "E227", {"start": v(-1.89, 21.19) * mm, "end": v(28, 21.19) * mm, "construction": true});
            skPoint(sketch, "E227.startSnap0", {"position": v(0, 21.19) * mm});
            skPoint(sketch, "E227.endSnap0", {"position": v(26.46, 21.19) * mm});
            skCircle(sketch, "E228", {"center": v(13.24, 21.19) * mm, "radius": 5.08 * mm});
            skLineSegment(sketch, "E229", {"start": v(13.24, 21.19) * mm, "end": v(13.24, 32.62) * mm});
            skCircle(sketch, "E230", {"center": v(13.24, 21.19) * mm, "radius": 2.54 * mm});
            skSolve(sketch);
        }
        {
            var Q0;
            {var subQ1=makeQuery(id+"F13.opExtrude","CAP_EDGE",EDGE,{"disambiguationData":[OSD([sQuery(id+"F12.wireOp",EDGE,"E177.left")])],"isStart":false});Q0=makeQuery(id+"F14.imprint","IMPRINT",FACE,{"disambiguationData":[TD([[makeQuery(id+"F14.imprint","IMPRINT",EDGE,{"derivedFrom":subQ1}),1.0]])]});}
            var Q1;
            {var subQ0=sQuery(id+"F14.wireOp",EDGE,"E224.right");var subQ1=sQuery(id+"F14.wireOp",EDGE,"E224.top");var subQ2=makeQuery(id+"F14.imprint","INTERSECT",VERTEX,{"derivedFrom":[subQ1,subQ0]});Q1=makeQuery(id+"F14.imprint","IMPRINT",FACE,{"disambiguationData":[TD([[makeQuery(id+"F14.imprint","IMPRINT",EDGE,{"disambiguationData":[TD([[subQ2,1.0]])],"derivedFrom":subQ1}),-1.0]])]});}
            var Q2;
            {var subQ6=makeQuery(id+"F13.opExtrude","CAP_EDGE",EDGE,{"disambiguationData":[OSD([sQuery(id+"F12.wireOp",EDGE,"E177.left")])],"isStart":false});Q2=makeQuery(id+"F14.imprint","IMPRINT",FACE,{"disambiguationData":[TD([[makeQuery(id+"F14.imprint","IMPRINT",EDGE,{"derivedFrom":subQ6}),-1.0]])]});}
            var Q3;
            {var subQ0=sQuery(id+"F14.wireOp",EDGE,"E226.right");Q3=makeQuery(id+"F14.imprint","IMPRINT",FACE,{"disambiguationData":[TD([[makeQuery(id+"F14.imprint","IMPRINT",EDGE,{"derivedFrom":subQ0}),1.0]])]});}
            var Q4;
            {var subQ0=sQuery(id+"F14.wireOp",EDGE,"E230");var subQ1=sQuery(id+"F14.wireOp",EDGE,"E225");var subQ2=makeQuery(id+"F14.imprint","INTERSECT",VERTEX,{"disambiguationData":[OD(1.0)],"derivedFrom":[subQ1,subQ0]});Q4=makeQuery(id+"F14.imprint","IMPRINT",FACE,{"disambiguationData":[TD([[makeQuery(id+"F14.imprint","IMPRINT",EDGE,{"disambiguationData":[TD([[subQ2,-1.0]])],"derivedFrom":subQ1}),1.0]])]});}
            var Q5;
            {var subQ0=sQuery(id+"F14.wireOp",EDGE,"E228");var subQ1=sQuery(id+"F14.wireOp",EDGE,"E225");var subQ2=makeQuery(id+"F14.imprint","INTERSECT",VERTEX,{"disambiguationData":[OD(1.0)],"derivedFrom":[subQ1,subQ0]});Q5=makeQuery(id+"F14.imprint","IMPRINT",FACE,{"disambiguationData":[TD([[makeQuery(id+"F14.imprint","IMPRINT",EDGE,{"disambiguationData":[TD([[subQ2,-1.0]])],"derivedFrom":subQ1}),1.0]])]});}
            var Q6;
            {var subQ0=sQuery(id+"F14.wireOp",EDGE,"E229");var subQ1=sQuery(id+"F14.wireOp",EDGE,"E225");var subQ2=makeQuery(id+"F14.imprint","INTERSECT",VERTEX,{"derivedFrom":[subQ1,subQ0]});Q6=makeQuery(id+"F14.imprint","IMPRINT",FACE,{"disambiguationData":[TD([[makeQuery(id+"F14.imprint","IMPRINT",EDGE,{"disambiguationData":[TD([[subQ2,-1.0]])],"derivedFrom":subQ1}),1.0]])]});}
            var Q7;
            {var subQ0=sQuery(id+"F14.wireOp",EDGE,"E229");var subQ1=sQuery(id+"F14.wireOp",EDGE,"E225");var subQ2=makeQuery(id+"F14.imprint","INTERSECT",VERTEX,{"derivedFrom":[subQ1,subQ0]});Q7=makeQuery(id+"F14.imprint","IMPRINT",FACE,{"disambiguationData":[TD([[makeQuery(id+"F14.imprint","IMPRINT",EDGE,{"disambiguationData":[TD([[subQ2,1.0]])],"derivedFrom":subQ1}),1.0]])]});}
            var Q8;
            {var subQ0=sQuery(id+"F14.wireOp",EDGE,"E225");var subQ1=makeQuery(id+"F14.imprint","INTERSECT",VERTEX,{"derivedFrom":[subQ0,sQuery(id+"F14.wireOp",EDGE,"E229")]});Q8=makeQuery(id+"F14.imprint","IMPRINT",FACE,{"disambiguationData":[TD([[makeQuery(id+"F14.imprint","IMPRINT",EDGE,{"disambiguationData":[TD([[subQ1,1.0]])],"derivedFrom":subQ0}),-1.0]])]});}
            var Q9;
            {var subQ0=sQuery(id+"F14.wireOp",EDGE,"E228");var subQ1=sQuery(id+"F14.wireOp",EDGE,"E225");var subQ4=makeQuery(id+"F14.imprint","INTERSECT",VERTEX,{"disambiguationData":[OD(0.0)],"derivedFrom":[subQ1,subQ0]});Q9=makeQuery(id+"F14.imprint","IMPRINT",FACE,{"disambiguationData":[TD([[makeQuery(id+"F14.imprint","IMPRINT",EDGE,{"disambiguationData":[TD([[subQ4,-1.0]])],"derivedFrom":subQ1}),-1.0]])]});}
            var Q10;
            {var subQ0=sQuery(id+"F14.wireOp",EDGE,"E226.bottom");var subQ1=sQuery(id+"F14.wireOp",EDGE,"E225");var subQ2=makeQuery(id+"F14.imprint","INTERSECT",VERTEX,{"derivedFrom":[subQ1,subQ0]});Q10=makeQuery(id+"F14.imprint","IMPRINT",FACE,{"disambiguationData":[TD([[makeQuery(id+"F14.imprint","IMPRINT",EDGE,{"disambiguationData":[TD([[subQ2,-1.0]])],"derivedFrom":subQ1}),-1.0]])]});}
            var Q11;
            {var subQ1=sQuery(id+"F14.wireOp",EDGE,"E224.right");var subQ3=sQuery(id+"F14.wireOp",EDGE,"E225");var subQ4=makeQuery(id+"F14.imprint","INTERSECT",VERTEX,{"derivedFrom":[subQ1,subQ3]});Q11=makeQuery(id+"F14.imprint","IMPRINT",FACE,{"disambiguationData":[TD([[makeQuery(id+"F14.imprint","IMPRINT",EDGE,{"disambiguationData":[TD([[subQ4,1.0]])],"derivedFrom":subQ3}),-1.0]])]});}
            extrude(context, id + "F15", {"entities" : qUnion([Q0, Q1, Q2, Q3, Q4, Q5, Q6, Q7, Q8, Q9, Q10, Q11]), "operationType" : NewBodyOperationType.REMOVE, "oppositeDirection" : true, "depth" : 25.4 * mm});
        }
        {
            var Q0;
            Q0=makeQuery(id+"F15.boolean.opBoolean","INTERSECT",EDGE,{"derivedFrom":[makeQuery(id+"F13.opExtrude","SWEPT_FACE",FACE,{"disambiguationData":[OSD([sQuery(id+"F12.wireOp",EDGE,"E210.top"),sQuery(id+"F12.wireOp",EDGE,"E211.bottom")])]}),makeQuery(id+"F15.opExtrude","SWEPT_FACE",FACE,{"disambiguationData":[OSD([sQuery(id+"F14.wireOp",EDGE,"E225")])]})]});
            var Q1;
            Q1=makeQuery(id+"F15.boolean.opBoolean","INTERSECT",EDGE,{"derivedFrom":[makeQuery(id+"F13.opExtrude","SWEPT_FACE",FACE,{"disambiguationData":[OSD([sQuery(id+"F12.wireOp",EDGE,"E212.top"),sQuery(id+"F12.wireOp",EDGE,"E213.bottom")])]}),makeQuery(id+"F15.opExtrude","SWEPT_FACE",FACE,{"disambiguationData":[OSD([sQuery(id+"F14.wireOp",EDGE,"E225")])]})]});
            fillet(context, id + "F16", {"entities" : qUnion([Q0, Q1]), "radius" : 0.76 * mm, "tangentPropagation" : true, "allowEdgeOverflow" : false});
        }
        {
            var Q0;
            Q0=makeQuery(id+"F15.boolean.opBoolean","COPY",FACE,{"disambiguationData":[TD([makeQuery(id+"F13.opExtrude","SWEPT_FACE",FACE,{"disambiguationData":[OSD([sQuery(id+"F12.wireOp",EDGE,"E187")])]})])],"derivedFrom":makeQuery(id+"F15.opExtrude","SWEPT_FACE",FACE,{"disambiguationData":[OSD([sQuery(id+"F14.wireOp",EDGE,"E229")])]})});
            var sketch = newSketch(context, id + "F17", { "sketchPlane" : qUnion([Q0])});
            skCircle(sketch, "E231", {"center": v(-98.31, 29.62) * mm, "radius": 1.98 * mm});
            skSolve(sketch);
        }
        {
            var Q0;
            Q0 = qSketchRegion(id + "F17", true);
            extrude(context, id + "F18", {"entities" : qUnion([Q0]), "operationType" : NewBodyOperationType.REMOVE, "oppositeDirection" : true, "depth" : 6.35 * mm, "offsetDistance" : 25.4 * mm});
        }
        {
            var Q0;
            Q0=makeQuery(id+"F15.boolean.opBoolean","COPY",FACE,{"disambiguationData":[TD([makeQuery(id+"F13.opExtrude","SWEPT_FACE",FACE,{"disambiguationData":[OSD([sQuery(id+"F12.wireOp",EDGE,"E188")])]})])],"derivedFrom":makeQuery(id+"F15.opExtrude","SWEPT_FACE",FACE,{"disambiguationData":[OSD([sQuery(id+"F14.wireOp",EDGE,"E229")])]})});
            var sketch = newSketch(context, id + "F19", { "sketchPlane" : qUnion([Q0])});
            skCircle(sketch, "E232", {"center": v(-83.85, 29.62) * mm, "radius": 1.98 * mm});
            skSolve(sketch);
        }
        {
            var Q0;
            Q0 = qSketchRegion(id + "F19", true);
            extrude(context, id + "F20", {"entities" : qUnion([Q0]), "operationType" : NewBodyOperationType.REMOVE, "oppositeDirection" : true, "depth" : 6.35 * mm, "offsetDistance" : 25.4 * mm});
        }
        {
            var Q0;
            Q0=qCreatedBy(makeId("Front.planeOp"),FACE);
            var sketch = newSketch(context, id + "F21", { "sketchPlane" : qUnion([Q0])});
            skArc(sketch, "E233", {"start": v(-134.93, 29.27) * mm, "mid": v(-134.35, 13.41) * mm, "end": v(-133.76, 29.27) * mm});
            skCircle(sketch, "E234", {"center": v(-134.35, 21.35) * mm, "radius": 9.53 * mm, "construction": true});
            skLineSegment(sketch, "E235", {"start": v(-146.46, 21.35) * mm, "end": v(-120.7, 21.35) * mm, "construction": true});
            skLineSegment(sketch, "E236", {"start": v(-134.35, 34.23) * mm, "end": v(-134.35, 9.48) * mm, "construction": true});
            skLineSegment(sketch, "E237", {"start": v(-126.41, 21.35) * mm, "end": v(-126.41, 23.73) * mm, "construction": true});
            skLineSegment(sketch, "E238", {"start": v(-124.82, 21.35) * mm, "end": v(-124.82, 23.73) * mm, "construction": true});
            skLineSegment(sketch, "E239.bottom", {"start": v(-143.87, 21.35) * mm, "end": v(-124.82, 21.35) * mm});
            skLineSegment(sketch, "E239.top", {"start": v(-143.87, 32.46) * mm, "end": v(-124.82, 32.46) * mm});
            skLineSegment(sketch, "E239.right", {"start": v(-124.82, 21.35) * mm, "end": v(-124.82, 23.73) * mm});
            skLineSegment(sketch, "E240.top", {"start": v(-143.87, 10.24) * mm, "end": v(-124.82, 10.24) * mm});
            skLineSegment(sketch, "E240.left", {"start": v(-143.87, 16.27) * mm, "end": v(-143.87, 10.24) * mm});
            skLineSegment(sketch, "E240.right", {"start": v(-124.82, 16.27) * mm, "end": v(-124.82, 10.24) * mm});
            skLineSegment(sketch, "E241", {"start": v(-134.35, 30.88) * mm, "end": v(-129.12, 30.88) * mm, "construction": true});
            skLineSegment(sketch, "E242", {"start": v(-138.32, 11.83) * mm, "end": v(-134.35, 11.83) * mm, "construction": true});
            skLineSegment(sketch, "E243", {"start": v(-134.35, 21.35) * mm, "end": v(-143.87, 32.46) * mm, "construction": true});
            skLineSegment(sketch, "E244", {"start": v(-134.35, 21.35) * mm, "end": v(-124.82, 32.46) * mm, "construction": true});
            skLineSegment(sketch, "E245", {"start": v(-134.35, 21.35) * mm, "end": v(-124.82, 10.24) * mm, "construction": true});
            skLineSegment(sketch, "E246", {"start": v(-134.35, 21.35) * mm, "end": v(-143.87, 10.24) * mm, "construction": true});
            skCircle(sketch, "E247", {"center": v(-134.35, 21.35) * mm, "radius": 11.11 * mm, "construction": true});
            skLineSegment(sketch, "E248", {"start": v(-123.24, 21.35) * mm, "end": v(-123.24, 18.66) * mm, "construction": true});
            skLineSegment(sketch, "E249", {"start": v(-126.41, 21.35) * mm, "end": v(-126.41, 18.68) * mm, "construction": true});
            skCircle(sketch, "E250", {"center": v(-141.58, 29.79) * mm, "radius": 1.2 * mm});
            skCircle(sketch, "E251", {"center": v(-127.12, 29.79) * mm, "radius": 1.2 * mm});
            skCircle(sketch, "E252", {"center": v(-141.58, 29.79) * mm, "radius": 1.98 * mm});
            skCircle(sketch, "E253", {"center": v(-127.12, 29.79) * mm, "radius": 1.98 * mm});
            skLineSegment(sketch, "E254", {"start": v(-134.35, 30.88) * mm, "end": v(-139.42, 30.88) * mm, "construction": true});
            skCircle(sketch, "E255", {"center": v(-138.16, 30.88) * mm, "radius": 0.6 * mm});
            skCircle(sketch, "E256", {"center": v(-130.54, 30.88) * mm, "radius": 0.6 * mm});
            skLineSegment(sketch, "E257", {"start": v(-141.58, 29.79) * mm, "end": v(-144.86, 26.98) * mm, "construction": true});
            skLineSegment(sketch, "E258", {"start": v(-127.12, 29.79) * mm, "end": v(-124.28, 27.36) * mm, "construction": true});
            skLineSegment(sketch, "E259", {"start": v(-141.58, 29.79) * mm, "end": v(-143.87, 32.46) * mm});
            skLineSegment(sketch, "E260", {"start": v(-127.12, 29.79) * mm, "end": v(-124.82, 32.46) * mm});
            skLineSegment(sketch, "E261", {"start": v(-127.12, 29.79) * mm, "end": v(-124.82, 27.82) * mm});
            skLineSegment(sketch, "E262", {"start": v(-141.58, 29.79) * mm, "end": v(-143.87, 27.82) * mm});
            skLineSegment(sketch, "E263", {"start": v(-141.58, 29.79) * mm, "end": v(-139.51, 27.38) * mm});
            skLineSegment(sketch, "E264", {"start": v(-127.12, 29.79) * mm, "end": v(-129.18, 27.38) * mm});
            skCircle(sketch, "E265", {"center": v(-134.35, 21.35) * mm, "radius": 10.32 * mm, "construction": true});
            skLineSegment(sketch, "E266", {"start": v(-134.35, 11.03) * mm, "end": v(-131.73, 11.03) * mm, "construction": true});
            skCircle(sketch, "E267", {"center": v(-127.63, 13.52) * mm, "radius": 1.2 * mm});
            skCircle(sketch, "E268", {"center": v(-141.06, 13.52) * mm, "radius": 1.2 * mm});
            skCircle(sketch, "E269", {"center": v(-127.63, 13.52) * mm, "radius": 1.98 * mm});
            skCircle(sketch, "E270", {"center": v(-141.06, 13.52) * mm, "radius": 1.98 * mm});
            skLineSegment(sketch, "E271", {"start": v(-138.8, 13.52) * mm, "end": v(-143.45, 13.52) * mm, "construction": true});
            skLineSegment(sketch, "E272", {"start": v(-125.4, 13.52) * mm, "end": v(-129.94, 13.52) * mm, "construction": true});
            skLineSegment(sketch, "E273.bottom", {"start": v(-142.25, 13.52) * mm, "end": v(-141.06, 13.52) * mm});
            skLineSegment(sketch, "E273.top", {"start": v(-142.25, 12.33) * mm, "end": v(-141.06, 12.33) * mm});
            skLineSegment(sketch, "E273.left", {"start": v(-142.25, 13.52) * mm, "end": v(-142.25, 12.33) * mm});
            skLineSegment(sketch, "E273.right", {"start": v(-141.06, 13.52) * mm, "end": v(-141.06, 12.33) * mm});
            skLineSegment(sketch, "E274.bottom", {"start": v(-141.06, 12.33) * mm, "end": v(-139.87, 12.33) * mm});
            skLineSegment(sketch, "E274.top", {"start": v(-141.06, 13.52) * mm, "end": v(-139.87, 13.52) * mm});
            skLineSegment(sketch, "E274.left", {"start": v(-141.06, 12.33) * mm, "end": v(-141.06, 13.52) * mm});
            skLineSegment(sketch, "E274.right", {"start": v(-139.87, 12.33) * mm, "end": v(-139.87, 13.52) * mm});
            skLineSegment(sketch, "E275.bottom", {"start": v(-128.82, 13.52) * mm, "end": v(-127.63, 13.52) * mm});
            skLineSegment(sketch, "E275.top", {"start": v(-128.82, 12.33) * mm, "end": v(-127.63, 12.33) * mm});
            skLineSegment(sketch, "E275.left", {"start": v(-128.82, 13.52) * mm, "end": v(-128.82, 12.33) * mm});
            skLineSegment(sketch, "E275.right", {"start": v(-127.63, 13.52) * mm, "end": v(-127.63, 12.33) * mm});
            skLineSegment(sketch, "E276.bottom", {"start": v(-127.63, 12.33) * mm, "end": v(-126.44, 12.33) * mm});
            skLineSegment(sketch, "E276.top", {"start": v(-127.63, 13.52) * mm, "end": v(-126.44, 13.52) * mm});
            skLineSegment(sketch, "E276.left", {"start": v(-127.63, 12.33) * mm, "end": v(-127.63, 13.52) * mm});
            skLineSegment(sketch, "E276.right", {"start": v(-126.44, 12.33) * mm, "end": v(-126.44, 13.52) * mm});
            skLineSegment(sketch, "E277", {"start": v(-134.35, 11.83) * mm, "end": v(-129.48, 11.83) * mm, "construction": true});
            skCircle(sketch, "E278", {"center": v(-137.52, 11.83) * mm, "radius": 0.64 * mm});
            skCircle(sketch, "E279", {"center": v(-131.17, 11.83) * mm, "radius": 0.64 * mm});
            skLineSegment(sketch, "E280", {"start": v(-134.35, 30.88) * mm, "end": v(-133.76, 29.27) * mm});
            skLineSegment(sketch, "E281", {"start": v(-134.35, 30.88) * mm, "end": v(-134.93, 29.27) * mm});
            skLineSegment(sketch, "E282.bottom", {"start": v(-143.87, 26.43) * mm, "end": v(-143.36, 26.43) * mm});
            skLineSegment(sketch, "E282.top", {"start": v(-143.87, 16.27) * mm, "end": v(-143.36, 16.27) * mm});
            skLineSegment(sketch, "E282.right", {"start": v(-143.36, 26.43) * mm, "end": v(-143.36, 16.27) * mm});
            skPoint(sketch, "E283.firstSnap0", {"position": v(-143.62, 26.43) * mm});
            skLineSegment(sketch, "E283.bottom", {"start": v(-124.82, 26.43) * mm, "end": v(-125.33, 26.43) * mm});
            skLineSegment(sketch, "E283.top", {"start": v(-124.82, 16.27) * mm, "end": v(-125.33, 16.27) * mm});
            skLineSegment(sketch, "E283.right", {"start": v(-125.33, 26.43) * mm, "end": v(-125.33, 16.27) * mm});
            skLineSegment(sketch, "E284.trimOffspring", {"start": v(-143.87, 26.43) * mm, "end": v(-143.87, 27.82) * mm});
            skLineSegment(sketch, "E285.trimOffspring", {"start": v(-124.82, 26.43) * mm, "end": v(-124.82, 27.82) * mm});
            skLineSegment(sketch, "E286", {"start": v(-134.35, 30.88) * mm, "end": v(-134.35, 32.46) * mm});
            skSolve(sketch);
        }
        {
            var Q0;
            {var subQ0=sQuery(id+"F21.wireOp",EDGE,"E262");var subQ1=sQuery(id+"F21.wireOp",EDGE,"E250");var subQ2=makeQuery(id+"F21.imprint","INTERSECT",VERTEX,{"derivedFrom":[subQ1,subQ0]});Q0=makeQuery(id+"F21.imprint","IMPRINT",FACE,{"disambiguationData":[TD([[makeQuery(id+"F21.imprint","IMPRINT",EDGE,{"disambiguationData":[TD([[subQ2,1.0]])],"derivedFrom":subQ1}),-1.0]])]});}
            var Q1;
            {var subQ0=sQuery(id+"F21.wireOp",EDGE,"E260");var subQ1=sQuery(id+"F21.wireOp",EDGE,"E251");var subQ2=makeQuery(id+"F21.imprint","INTERSECT",VERTEX,{"derivedFrom":[subQ1,subQ0]});Q1=makeQuery(id+"F21.imprint","IMPRINT",FACE,{"disambiguationData":[TD([[makeQuery(id+"F21.imprint","IMPRINT",EDGE,{"disambiguationData":[TD([[subQ2,1.0]])],"derivedFrom":subQ1}),-1.0]])]});}
            var Q2;
            {var subQ6=sQuery(id+"F21.wireOp",EDGE,"E282.bottom");Q2=makeQuery(id+"F21.imprint","IMPRINT",FACE,{"disambiguationData":[TD([[makeQuery(id+"F21.imprint","IMPRINT",EDGE,{"derivedFrom":subQ6}),1.0]])]});}
            var Q3;
            {var subQ12=sQuery(id+"F21.wireOp",EDGE,"E283.bottom");Q3=makeQuery(id+"F21.imprint","IMPRINT",FACE,{"disambiguationData":[TD([[makeQuery(id+"F21.imprint","IMPRINT",EDGE,{"derivedFrom":subQ12}),-1.0]])]});}
            var Q4;
            {var subQ0=sQuery(id+"F21.wireOp",EDGE,"E262");var subQ1=sQuery(id+"F21.wireOp",EDGE,"E250");var subQ2=makeQuery(id+"F21.imprint","INTERSECT",VERTEX,{"derivedFrom":[subQ1,subQ0]});Q4=makeQuery(id+"F21.imprint","IMPRINT",FACE,{"disambiguationData":[TD([[makeQuery(id+"F21.imprint","IMPRINT",EDGE,{"disambiguationData":[TD([[subQ2,-1.0]])],"derivedFrom":subQ1}),-1.0]])]});}
            var Q5;
            {var subQ0=sQuery(id+"F21.wireOp",EDGE,"E259");var subQ1=sQuery(id+"F21.wireOp",EDGE,"E250");var subQ2=makeQuery(id+"F21.imprint","INTERSECT",VERTEX,{"derivedFrom":[subQ1,subQ0]});Q5=makeQuery(id+"F21.imprint","IMPRINT",FACE,{"disambiguationData":[TD([[makeQuery(id+"F21.imprint","IMPRINT",EDGE,{"disambiguationData":[TD([[subQ2,1.0]])],"derivedFrom":subQ1}),-1.0]])]});}
            var Q6;
            {var subQ0=sQuery(id+"F21.wireOp",EDGE,"E264");var subQ1=sQuery(id+"F21.wireOp",EDGE,"E251");var subQ2=makeQuery(id+"F21.imprint","INTERSECT",VERTEX,{"derivedFrom":[subQ1,subQ0]});Q6=makeQuery(id+"F21.imprint","IMPRINT",FACE,{"disambiguationData":[TD([[makeQuery(id+"F21.imprint","IMPRINT",EDGE,{"disambiguationData":[TD([[subQ2,1.0]])],"derivedFrom":subQ1}),-1.0]])]});}
            var Q7;
            {var subQ0=sQuery(id+"F21.wireOp",EDGE,"E264");var subQ1=sQuery(id+"F21.wireOp",EDGE,"E251");var subQ2=makeQuery(id+"F21.imprint","INTERSECT",VERTEX,{"derivedFrom":[subQ1,subQ0]});Q7=makeQuery(id+"F21.imprint","IMPRINT",FACE,{"disambiguationData":[TD([[makeQuery(id+"F21.imprint","IMPRINT",EDGE,{"disambiguationData":[TD([[subQ2,-1.0]])],"derivedFrom":subQ1}),-1.0]])]});}
            var Q8;
            Q8=makeQuery(id+"F21.imprint","IMPRINT",FACE,{"disambiguationData":[TD([[makeQuery(id+"F21.imprint","IMPRINT",EDGE,{"derivedFrom":sQuery(id+"F21.wireOp",EDGE,"E240.top")}),1.0]])]});
            var Q9;
            Q9=makeQuery(id+"F21.imprint","IMPRINT",FACE,{"disambiguationData":[TD([[makeQuery(id+"F21.imprint","IMPRINT",EDGE,{"derivedFrom":sQuery(id+"F21.wireOp",EDGE,"E270")}),1.0]])]});
            var Q10;
            Q10=makeQuery(id+"F21.imprint","IMPRINT",FACE,{"disambiguationData":[TD([[makeQuery(id+"F21.imprint","IMPRINT",EDGE,{"derivedFrom":sQuery(id+"F21.wireOp",EDGE,"E269")}),1.0]])]});
            extrude(context, id + "F22", {"entities" : qUnion([Q0, Q1, Q2, Q3, Q4, Q5, Q6, Q7, Q8, Q9, Q10]), "depth" : 0.25 * mm});
        }
        {
            var Q0;
            Q0=makeQuery(id+"F22.opExtrude","CAP_FACE",FACE,{"disambiguationData":[OSD([sQuery(id+"F21.wireOp",EDGE,"E233"),sQuery(id+"F21.wireOp",EDGE,"E240.top"),sQuery(id+"F21.wireOp",EDGE,"E240.left"),sQuery(id+"F21.wireOp",EDGE,"E240.right"),sQuery(id+"F21.wireOp",EDGE,"E250"),sQuery(id+"F21.wireOp",EDGE,"E251"),sQuery(id+"F21.wireOp",EDGE,"E252"),sQuery(id+"F21.wireOp",EDGE,"E253"),sQuery(id+"F21.wireOp",EDGE,"E261"),sQuery(id+"F21.wireOp",EDGE,"E262"),sQuery(id+"F21.wireOp",EDGE,"E263"),sQuery(id+"F21.wireOp",EDGE,"E264"),sQuery(id+"F21.wireOp",EDGE,"E267"),sQuery(id+"F21.wireOp",EDGE,"E268"),sQuery(id+"F21.wireOp",EDGE,"E273.top"),sQuery(id+"F21.wireOp",EDGE,"E273.left"),sQuery(id+"F21.wireOp",EDGE,"E274.bottom"),sQuery(id+"F21.wireOp",EDGE,"E274.right"),sQuery(id+"F21.wireOp",EDGE,"E275.top"),sQuery(id+"F21.wireOp",EDGE,"E275.left"),sQuery(id+"F21.wireOp",EDGE,"E276.bottom"),sQuery(id+"F21.wireOp",EDGE,"E276.right"),sQuery(id+"F21.wireOp",EDGE,"E278"),sQuery(id+"F21.wireOp",EDGE,"E279"),sQuery(id+"F21.wireOp",EDGE,"E282.bottom"),sQuery(id+"F21.wireOp",EDGE,"E282.top"),sQuery(id+"F21.wireOp",EDGE,"E282.right"),sQuery(id+"F21.wireOp",EDGE,"E283.bottom"),sQuery(id+"F21.wireOp",EDGE,"E283.top"),sQuery(id+"F21.wireOp",EDGE,"E283.right"),sQuery(id+"F21.wireOp",EDGE,"E284.trimOffspring"),sQuery(id+"F21.wireOp",EDGE,"E285.trimOffspring")])],"isStart":false});
            var sketch = newSketch(context, id + "F23", { "sketchPlane" : qUnion([Q0])});
            skArc(sketch, "E287", {"start": v(-139.51, 27.38) * mm, "mid": v(-134.35, 13.41) * mm, "end": v(-129.18, 27.38) * mm});
            skPoint(sketch, "E288.oppositeSnap0", {"position": v(-127.27, 31.77) * mm});
            skLineSegment(sketch, "E288.bottom", {"start": v(-143.87, 10.24) * mm, "end": v(-124.82, 10.24) * mm});
            skLineSegment(sketch, "E288.top", {"start": v(-141.73, 31.77) * mm, "end": v(-141.43, 31.77) * mm});
            skLineSegment(sketch, "E288.left", {"start": v(-143.87, 10.24) * mm, "end": v(-143.87, 16.27) * mm});
            skLineSegment(sketch, "E288.right", {"start": v(-124.82, 10.24) * mm, "end": v(-124.82, 16.27) * mm});
            skLineSegment(sketch, "E289.bottom", {"start": v(-143.87, 26.43) * mm, "end": v(-143.36, 26.43) * mm});
            skLineSegment(sketch, "E289.top", {"start": v(-143.87, 16.27) * mm, "end": v(-143.36, 16.27) * mm});
            skLineSegment(sketch, "E289.right", {"start": v(-143.36, 26.43) * mm, "end": v(-143.36, 16.27) * mm});
            skLineSegment(sketch, "E290.bottom", {"start": v(-124.82, 26.43) * mm, "end": v(-125.33, 26.43) * mm});
            skLineSegment(sketch, "E290.top", {"start": v(-124.82, 16.27) * mm, "end": v(-125.33, 16.27) * mm});
            skLineSegment(sketch, "E290.right", {"start": v(-125.33, 26.43) * mm, "end": v(-125.33, 16.27) * mm});
            skCircle(sketch, "E291", {"center": v(-141.06, 13.52) * mm, "radius": 1.2 * mm});
            skCircle(sketch, "E292", {"center": v(-127.63, 13.52) * mm, "radius": 1.2 * mm});
            skCircle(sketch, "E293", {"center": v(-137.52, 11.83) * mm, "radius": 0.5 * mm});
            skCircle(sketch, "E294", {"center": v(-131.17, 11.83) * mm, "radius": 0.5 * mm});
            skLineSegment(sketch, "E295", {"start": v(-143.87, 26.43) * mm, "end": v(-143.87, 27.82) * mm});
            skLineSegment(sketch, "E296", {"start": v(-143.87, 27.82) * mm, "end": v(-143.09, 28.5) * mm});
            skLineSegment(sketch, "E297", {"start": v(-140.29, 28.28) * mm, "end": v(-139.51, 27.38) * mm});
            skLineSegment(sketch, "E298", {"start": v(-129.18, 27.38) * mm, "end": v(-128.4, 28.28) * mm});
            skLineSegment(sketch, "E299", {"start": v(-124.82, 26.43) * mm, "end": v(-124.82, 27.82) * mm});
            skLineSegment(sketch, "E300", {"start": v(-124.82, 27.82) * mm, "end": v(-125.6, 28.5) * mm});
            skCircle(sketch, "E301", {"center": v(-141.58, 29.79) * mm, "radius": 1.2 * mm});
            skCircle(sketch, "E302", {"center": v(-127.12, 29.79) * mm, "radius": 1.2 * mm});
            skArc(sketch, "E303", {"start": v(-140.29, 28.28) * mm, "mid": v(-141.43, 31.77) * mm, "end": v(-143.09, 28.5) * mm});
            skArc(sketch, "E304", {"start": v(-125.6, 28.5) * mm, "mid": v(-127.27, 31.77) * mm, "end": v(-128.4, 28.28) * mm});
            skLineSegment(sketch, "E305.trimOffspring", {"start": v(-127.27, 31.77) * mm, "end": v(-126.96, 31.77) * mm});
            skPoint(sketch, "E306.orphan", {"position": v(-124.82, 31.77) * mm});
            skSolve(sketch);
        }
        {
            var Q0;
            Q0 = qSketchRegion(id + "F23", true);
            extrude(context, id + "F24", {"entities" : qUnion([Q0]), "operationType" : NewBodyOperationType.ADD, "depth" : 25.4 * mm});
        }
        {
            var Q0;
            Q0=makeQuery(id+"F24.boolean.opBoolean","MERGE",FACE,{"derivedFrom":[makeQuery(id+"F22.opExtrude","SWEPT_FACE",FACE,{"disambiguationData":[OSD([sQuery(id+"F21.wireOp",EDGE,"E240.left")])]}),makeQuery(id+"F22.opExtrude","SWEPT_FACE",FACE,{"disambiguationData":[OSD([sQuery(id+"F21.wireOp",EDGE,"E284.trimOffspring")])]}),makeQuery(id+"F24.opExtrude","SWEPT_FACE",FACE,{"disambiguationData":[OSD([sQuery(id+"F23.wireOp",EDGE,"E288.left")])]})]});
            var sketch = newSketch(context, id + "F25", { "sketchPlane" : qUnion([Q0])});
            skLineSegment(sketch, "E307", {"start": v(0.59, 10.24) * mm, "end": v(13.12, 13.67) * mm});
            skLineSegment(sketch, "E308", {"start": v(13.12, 13.67) * mm, "end": v(20.97, 21.45) * mm});
            skLineSegment(sketch, "E309", {"start": v(20.97, 21.45) * mm, "end": v(23.7, 31.19) * mm});
            skLineSegment(sketch, "E310", {"start": v(0, 32.13) * mm, "end": v(0, 33.67) * mm});
            skLineSegment(sketch, "E311", {"start": v(23.7, 31.19) * mm, "end": v(0, 32.13) * mm});
            skLineSegment(sketch, "E312", {"start": v(0, 33.67) * mm, "end": v(2.92, 35.76) * mm});
            skLineSegment(sketch, "E313", {"start": v(2.92, 35.76) * mm, "end": v(32.6, 35.76) * mm});
            skLineSegment(sketch, "E314", {"start": v(32.6, 35.76) * mm, "end": v(32.6, 7.44) * mm});
            skLineSegment(sketch, "E315", {"start": v(32.6, 7.44) * mm, "end": v(5.34, 7.44) * mm});
            skLineSegment(sketch, "E316", {"start": v(5.34, 7.44) * mm, "end": v(0.59, 10.24) * mm});
            skSolve(sketch);
        }
        {
            var Q0;
            Q0 = qSketchRegion(id + "F25", true);
            extrude(context, id + "F26", {"entities" : qUnion([Q0]), "operationType" : NewBodyOperationType.REMOVE, "oppositeDirection" : true, "depth" : 25.4 * mm});
        }
        {
            var Q0;
            Q0=makeQuery(id+"F22.opExtrude","SWEPT_BODY",BODY,{"disambiguationData":[OSD([sQuery(id+"F21.wireOp",EDGE,"E233"),sQuery(id+"F21.wireOp",EDGE,"E240.top"),sQuery(id+"F21.wireOp",EDGE,"E240.left"),sQuery(id+"F21.wireOp",EDGE,"E240.right"),sQuery(id+"F21.wireOp",EDGE,"E250"),sQuery(id+"F21.wireOp",EDGE,"E251"),sQuery(id+"F21.wireOp",EDGE,"E252"),sQuery(id+"F21.wireOp",EDGE,"E253"),sQuery(id+"F21.wireOp",EDGE,"E261"),sQuery(id+"F21.wireOp",EDGE,"E262"),sQuery(id+"F21.wireOp",EDGE,"E263"),sQuery(id+"F21.wireOp",EDGE,"E264"),sQuery(id+"F21.wireOp",EDGE,"E267"),sQuery(id+"F21.wireOp",EDGE,"E268"),sQuery(id+"F21.wireOp",EDGE,"E273.top"),sQuery(id+"F21.wireOp",EDGE,"E273.left"),sQuery(id+"F21.wireOp",EDGE,"E274.bottom"),sQuery(id+"F21.wireOp",EDGE,"E274.right"),sQuery(id+"F21.wireOp",EDGE,"E275.top"),sQuery(id+"F21.wireOp",EDGE,"E275.left"),sQuery(id+"F21.wireOp",EDGE,"E276.bottom"),sQuery(id+"F21.wireOp",EDGE,"E276.right"),sQuery(id+"F21.wireOp",EDGE,"E278"),sQuery(id+"F21.wireOp",EDGE,"E279"),sQuery(id+"F21.wireOp",EDGE,"E282.bottom"),sQuery(id+"F21.wireOp",EDGE,"E282.top"),sQuery(id+"F21.wireOp",EDGE,"E282.right"),sQuery(id+"F21.wireOp",EDGE,"E283.bottom"),sQuery(id+"F21.wireOp",EDGE,"E283.top"),sQuery(id+"F21.wireOp",EDGE,"E283.right"),sQuery(id+"F21.wireOp",EDGE,"E284.trimOffspring"),sQuery(id+"F21.wireOp",EDGE,"E285.trimOffspring")])]});
            deleteBodies(context, id + "F27", {"entities" : qUnion([Q0])});
        }
    });
